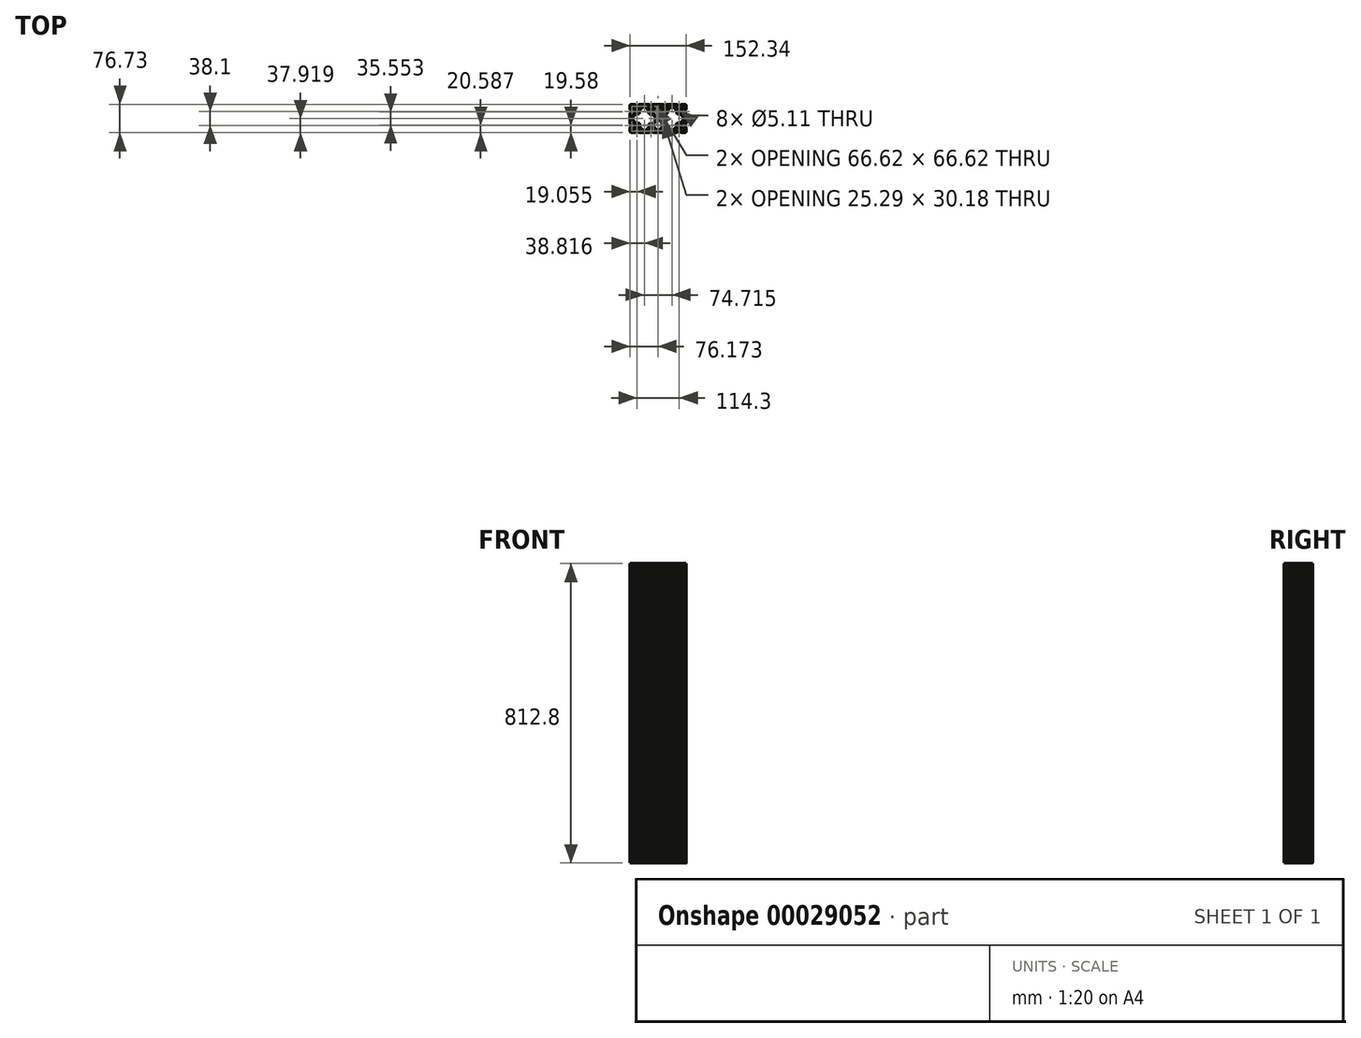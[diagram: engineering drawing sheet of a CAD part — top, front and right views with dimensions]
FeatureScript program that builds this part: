
annotation { "Feature Type Name" : "Feature", "Feature Type Description" : "" }
export const myFeature = defineFeature(function(context is Context, id is Id, definition is map)
    precondition{}
    {
        {
            var Q0;
            Q0=qCreatedBy(makeId("Top.planeOp"),FACE);
            var sketch = newSketch(context, id + "F0", { "sketchPlane" : qUnion([Q0])});
            skLineSegment(sketch, "E0", {"start": v(5.37, 0) * mm, "end": v(1.16, 0) * mm});
            skArc(sketch, "E1", {"start": v(0, 0) * mm, "mid": v(0.58, -0.58) * mm, "end": v(1.16, 0) * mm});
            skLineSegment(sketch, "E2", {"start": v(0, 0) * mm, "end": v(-4.73, 0) * mm});
            skArc(sketch, "E3", {"start": v(-5.9, 0) * mm, "mid": v(-5.3, -0.58) * mm, "end": v(-4.73, 0) * mm});
            skLineSegment(sketch, "E4", {"start": v(-5.9, 0) * mm, "end": v(-7.67, 0) * mm});
            skLineSegment(sketch, "E5", {"start": v(-7.53, -4.06) * mm, "end": v(-4.6, -4.06) * mm});
            skArc(sketch, "E6", {"start": v(-7.67, 0) * mm, "mid": v(-9.7, -2.1) * mm, "end": v(-7.53, -4.06) * mm});
            skLineSegment(sketch, "E7", {"start": v(-8.46, -10.87) * mm, "end": v(-3.58, -6) * mm});
            skArc(sketch, "E8", {"start": v(-3.58, -6) * mm, "mid": v(-3.37, -4.65) * mm, "end": v(-4.6, -4.06) * mm});
            skLineSegment(sketch, "E9", {"start": v(-11.33, -12.06) * mm, "end": v(-13.53, -12.06) * mm});
            skPoint(sketch, "E10.visualSharp", {"position": v(-9.65, -12.06) * mm});
            skArc(sketch, "E10.filletArc", {"start": v(-11.33, -12.06) * mm, "mid": v(-9.77, -11.75) * mm, "end": v(-8.46, -10.87) * mm});
            skArc(sketch, "E11.MirrorCS", {"start": v(-27.06, 0) * mm, "mid": v(-27.64, -0.58) * mm, "end": v(-28.22, 0) * mm});
            skArc(sketch, "E12.MirrorCS", {"start": v(-21.17, 0) * mm, "mid": v(-21.75, -0.58) * mm, "end": v(-22.33, 0) * mm});
            skPoint(sketch, "E13.MirrorP", {"position": v(-17.41, -12.06) * mm});
            skArc(sketch, "E14.MirrorCS", {"start": v(-15.73, -12.06) * mm, "mid": v(-17.28, -11.75) * mm, "end": v(-18.6, -10.87) * mm});
            skLineSegment(sketch, "E15.MirrorCS", {"start": v(-15.73, -12.06) * mm, "end": v(-13.53, -12.06) * mm});
            skArc(sketch, "E16.MirrorCS", {"start": v(-23.48, -6) * mm, "mid": v(-23.68, -4.65) * mm, "end": v(-22.46, -4.06) * mm});
            skLineSegment(sketch, "E17.MirrorCS", {"start": v(-18.6, -10.87) * mm, "end": v(-23.48, -6) * mm});
            skArc(sketch, "E18.MirrorCS", {"start": v(-19.4, 0) * mm, "mid": v(-17.36, -2.1) * mm, "end": v(-19.52, -4.06) * mm});
            skLineSegment(sketch, "E19.MirrorCS", {"start": v(-19.52, -4.06) * mm, "end": v(-22.46, -4.06) * mm});
            skLineSegment(sketch, "E20.MirrorCS", {"start": v(-27.06, 0) * mm, "end": v(-22.33, 0) * mm});
            skLineSegment(sketch, "E21.MirrorCS", {"start": v(-21.17, 0) * mm, "end": v(-19.4, 0) * mm});
            skLineSegment(sketch, "E22.MirrorCS", {"start": v(22.07, -12.06) * mm, "end": v(24.27, -12.06) * mm});
            skLineSegment(sketch, "E23.MirrorCS", {"start": v(26.47, -12.06) * mm, "end": v(24.27, -12.06) * mm});
            skArc(sketch, "E24.MirrorCS", {"start": v(22.07, -12.06) * mm, "mid": v(20.52, -11.75) * mm, "end": v(19.2, -10.87) * mm});
            skArc(sketch, "E25.MirrorCS", {"start": v(26.47, -12.06) * mm, "mid": v(28.03, -11.75) * mm, "end": v(29.35, -10.87) * mm});
            skPoint(sketch, "E26.MirrorP", {"position": v(20.39, -12.06) * mm});
            skPoint(sketch, "E27.MirrorP", {"position": v(28.16, -12.06) * mm});
            skArc(sketch, "E28.MirrorCS", {"start": v(16.63, 0) * mm, "mid": v(16.05, -0.58) * mm, "end": v(15.47, 0) * mm});
            skLineSegment(sketch, "E29.MirrorCS", {"start": v(16.63, 0) * mm, "end": v(18.4, 0) * mm});
            skArc(sketch, "E30.MirrorCS", {"start": v(31.91, 0) * mm, "mid": v(32.5, -0.58) * mm, "end": v(33.07, 0) * mm});
            skArc(sketch, "E31.MirrorCS", {"start": v(10.74, 0) * mm, "mid": v(10.16, -0.58) * mm, "end": v(9.58, 0) * mm});
            skArc(sketch, "E32.MirrorCS", {"start": v(14.32, -6) * mm, "mid": v(14.12, -4.65) * mm, "end": v(15.34, -4.06) * mm});
            skLineSegment(sketch, "E33.MirrorCS", {"start": v(31.91, 0) * mm, "end": v(30.14, 0) * mm});
            skArc(sketch, "E34.MirrorCS", {"start": v(37.8, 0) * mm, "mid": v(38.38, -0.58) * mm, "end": v(38.96, 0) * mm});
            skLineSegment(sketch, "E35.MirrorCS", {"start": v(10.74, 0) * mm, "end": v(15.47, 0) * mm});
            skLineSegment(sketch, "E36.MirrorCS", {"start": v(18.28, -4.06) * mm, "end": v(15.34, -4.06) * mm});
            skArc(sketch, "E37.MirrorCS", {"start": v(34.22, -6) * mm, "mid": v(34.43, -4.65) * mm, "end": v(33.2, -4.06) * mm});
            skLineSegment(sketch, "E38.MirrorCS", {"start": v(19.2, -10.87) * mm, "end": v(14.32, -6) * mm});
            skArc(sketch, "E39.MirrorCS", {"start": v(30.14, 0) * mm, "mid": v(28.1, -2.1) * mm, "end": v(30.27, -4.06) * mm});
            skLineSegment(sketch, "E40.MirrorCS", {"start": v(37.8, 0) * mm, "end": v(33.07, 0) * mm});
            skLineSegment(sketch, "E41.MirrorCS", {"start": v(5.37, 0) * mm, "end": v(9.58, 0) * mm});
            skLineSegment(sketch, "E42.MirrorCS", {"start": v(29.35, -10.87) * mm, "end": v(34.22, -6) * mm});
            skLineSegment(sketch, "E43.MirrorCS", {"start": v(43.17, 0) * mm, "end": v(38.96, 0) * mm});
            skLineSegment(sketch, "E44.MirrorCS", {"start": v(30.27, -4.06) * mm, "end": v(33.2, -4.06) * mm});
            skArc(sketch, "E45.MirrorCS", {"start": v(18.4, 0) * mm, "mid": v(20.44, -2.1) * mm, "end": v(18.28, -4.06) * mm});
            skArc(sketch, "E46.MirrorCS", {"start": v(108.22, 0) * mm, "mid": v(108.8, -0.58) * mm, "end": v(109.39, 0) * mm});
            skLineSegment(sketch, "E47.MirrorCS", {"start": v(108.22, 0) * mm, "end": v(106.45, 0) * mm});
            skArc(sketch, "E48.MirrorCS", {"start": v(114.11, 0) * mm, "mid": v(114.7, -0.58) * mm, "end": v(115.28, 0) * mm});
            skArc(sketch, "E49.MirrorCS", {"start": v(97.68, -12.06) * mm, "mid": v(96.12, -11.75) * mm, "end": v(94.8, -10.87) * mm});
            skLineSegment(sketch, "E50.MirrorCS", {"start": v(114.11, 0) * mm, "end": v(109.39, 0) * mm});
            skArc(sketch, "E51.MirrorCS", {"start": v(102.79, -12.06) * mm, "mid": v(104.34, -11.75) * mm, "end": v(105.66, -10.87) * mm});
            skArc(sketch, "E52.MirrorCS", {"start": v(106.45, 0) * mm, "mid": v(104.42, -2.1) * mm, "end": v(106.58, -4.06) * mm});
            skLineSegment(sketch, "E53.MirrorCS", {"start": v(106.58, -4.06) * mm, "end": v(109.52, -4.06) * mm});
            skArc(sketch, "E54.MirrorCS", {"start": v(110.54, -6) * mm, "mid": v(110.74, -4.65) * mm, "end": v(109.52, -4.06) * mm});
            skArc(sketch, "E55.MirrorCS", {"start": v(94.01, 0) * mm, "mid": v(96.04, -2.1) * mm, "end": v(93.88, -4.06) * mm});
            skLineSegment(sketch, "E56.MirrorCS", {"start": v(105.66, -10.87) * mm, "end": v(110.54, -6) * mm});
            skPoint(sketch, "E57.MirrorP", {"position": v(103.76, -12.06) * mm});
            skArc(sketch, "E58.MirrorCS", {"start": v(86.35, 0) * mm, "mid": v(85.76, -0.58) * mm, "end": v(85.18, 0) * mm});
            skArc(sketch, "E59.MirrorCS", {"start": v(92.24, 0) * mm, "mid": v(91.66, -0.58) * mm, "end": v(91.07, 0) * mm});
            skArc(sketch, "E60.MirrorCS", {"start": v(48.55, 0) * mm, "mid": v(47.96, -0.58) * mm, "end": v(47.38, 0) * mm});
            skArc(sketch, "E61.MirrorCS", {"start": v(54.44, 0) * mm, "mid": v(53.85, -0.58) * mm, "end": v(53.27, 0) * mm});
            skLineSegment(sketch, "E62.MirrorCS", {"start": v(86.35, 0) * mm, "end": v(91.07, 0) * mm});
            skLineSegment(sketch, "E63.MirrorCS", {"start": v(69.71, 0) * mm, "end": v(67.94, 0) * mm});
            skLineSegment(sketch, "E64.MirrorCS", {"start": v(43.17, 0) * mm, "end": v(47.38, 0) * mm});
            skArc(sketch, "E65.MirrorCS", {"start": v(69.71, 0) * mm, "mid": v(70.3, -0.58) * mm, "end": v(70.88, 0) * mm});
            skLineSegment(sketch, "E66.MirrorCS", {"start": v(92.24, 0) * mm, "end": v(94.01, 0) * mm});
            skLineSegment(sketch, "E67.MirrorCS", {"start": v(93.88, -4.06) * mm, "end": v(90.94, -4.06) * mm});
            skLineSegment(sketch, "E68.MirrorCS", {"start": v(94.8, -10.87) * mm, "end": v(89.92, -6) * mm});
            skArc(sketch, "E69.MirrorCS", {"start": v(75.6, 0) * mm, "mid": v(76.18, -0.58) * mm, "end": v(76.77, 0) * mm});
            skArc(sketch, "E70.MirrorCS", {"start": v(89.92, -6) * mm, "mid": v(89.72, -4.65) * mm, "end": v(90.94, -4.06) * mm});
            skLineSegment(sketch, "E71.MirrorCS", {"start": v(75.6, 0) * mm, "end": v(70.88, 0) * mm});
            skLineSegment(sketch, "E72.MirrorCS", {"start": v(48.55, 0) * mm, "end": v(53.27, 0) * mm});
            skArc(sketch, "E73.MirrorCS", {"start": v(64.27, -12.06) * mm, "mid": v(65.83, -11.75) * mm, "end": v(67.15, -10.87) * mm});
            skArc(sketch, "E74.MirrorCS", {"start": v(59.87, -12.06) * mm, "mid": v(58.32, -11.75) * mm, "end": v(57, -10.87) * mm});
            skLineSegment(sketch, "E75.MirrorCS", {"start": v(64.27, -12.06) * mm, "end": v(62.07, -12.06) * mm});
            skLineSegment(sketch, "E76.MirrorCS", {"start": v(54.44, 0) * mm, "end": v(56.21, 0) * mm});
            skLineSegment(sketch, "E77.MirrorCS", {"start": v(59.87, -12.06) * mm, "end": v(62.07, -12.06) * mm});
            skLineSegment(sketch, "E78.MirrorCS", {"start": v(56.08, -4.06) * mm, "end": v(53.14, -4.06) * mm});
            skArc(sketch, "E79.MirrorCS", {"start": v(52.12, -6) * mm, "mid": v(51.92, -4.65) * mm, "end": v(53.14, -4.06) * mm});
            skLineSegment(sketch, "E80.MirrorCS", {"start": v(68.07, -4.06) * mm, "end": v(71, -4.06) * mm});
            skLineSegment(sketch, "E81.MirrorCS", {"start": v(57, -10.87) * mm, "end": v(52.12, -6) * mm});
            skLineSegment(sketch, "E82.MirrorCS", {"start": v(67.15, -10.87) * mm, "end": v(72.03, -6) * mm});
            skArc(sketch, "E83.MirrorCS", {"start": v(56.21, 0) * mm, "mid": v(58.24, -2.1) * mm, "end": v(56.08, -4.06) * mm});
            skLineSegment(sketch, "E84.MirrorCS", {"start": v(80.97, 0) * mm, "end": v(76.77, 0) * mm});
            skLineSegment(sketch, "E85.MirrorCS", {"start": v(80.97, 0) * mm, "end": v(85.18, 0) * mm});
            skArc(sketch, "E86.MirrorCS", {"start": v(72.03, -6) * mm, "mid": v(72.23, -4.65) * mm, "end": v(71, -4.06) * mm});
            skArc(sketch, "E87.MirrorCS", {"start": v(67.94, 0) * mm, "mid": v(65.9, -2.1) * mm, "end": v(68.07, -4.06) * mm});
            skPoint(sketch, "E88.MirrorP", {"position": v(96, -12.06) * mm});
            skPoint(sketch, "E89.MirrorP", {"position": v(65.96, -12.06) * mm});
            skPoint(sketch, "E90.MirrorP", {"position": v(58.2, -12.06) * mm});
            skPoint(sketch, "E91.end.orphan", {"position": v(43.17, -22.8) * mm});
            skLineSegment(sketch, "E92", {"start": v(115.28, 0) * mm, "end": v(115.28, 0) * mm});
            skPoint(sketch, "E93.visualSharp", {"position": v(119.34, 0) * mm});
            skArc(sketch, "E93.filletArc", {"start": v(118.15, -1.2) * mm, "mid": v(116.83, -0.3) * mm, "end": v(115.28, 0) * mm});
            skLineSegment(sketch, "E94", {"start": v(97.68, -12.06) * mm, "end": v(102.79, -12.06) * mm});
            skArc(sketch, "E95.MirrorCS", {"start": v(119.34, -5.23) * mm, "mid": v(118.76, -4.65) * mm, "end": v(119.34, -4.06) * mm});
            skArc(sketch, "E96.MirrorCS", {"start": v(113.35, -29.42) * mm, "mid": v(114.69, -29.62) * mm, "end": v(115.28, -28.4) * mm});
            skLineSegment(sketch, "E97.MirrorCS", {"start": v(119.34, -11.12) * mm, "end": v(119.34, -12.9) * mm});
            skArc(sketch, "E98.MirrorCS", {"start": v(119.34, -11.12) * mm, "mid": v(118.76, -10.54) * mm, "end": v(119.34, -9.95) * mm});
            skLineSegment(sketch, "E99.MirrorCS", {"start": v(115.28, -25.46) * mm, "end": v(115.28, -28.4) * mm});
            skLineSegment(sketch, "E100.MirrorCS", {"start": v(119.34, -5.23) * mm, "end": v(119.34, -9.95) * mm});
            skArc(sketch, "E101.MirrorCS", {"start": v(119.34, -33) * mm, "mid": v(118.76, -33.58) * mm, "end": v(119.34, -34.16) * mm});
            skLineSegment(sketch, "E102.MirrorCS", {"start": v(115.28, -12.76) * mm, "end": v(115.28, -9.82) * mm});
            skArc(sketch, "E103.MirrorCS", {"start": v(107.28, -21.67) * mm, "mid": v(107.59, -23.22) * mm, "end": v(108.47, -24.54) * mm});
            skLineSegment(sketch, "E104.MirrorCS", {"start": v(119.34, -27.1) * mm, "end": v(119.34, -25.33) * mm});
            skLineSegment(sketch, "E105.MirrorCS", {"start": v(108.47, -13.68) * mm, "end": v(113.35, -8.8) * mm});
            skLineSegment(sketch, "E106.MirrorCS", {"start": v(119.34, -33) * mm, "end": v(119.34, -28.27) * mm});
            skArc(sketch, "E107.MirrorCS", {"start": v(113.35, -8.8) * mm, "mid": v(114.69, -8.6) * mm, "end": v(115.28, -9.82) * mm});
            skArc(sketch, "E108.MirrorCS", {"start": v(119.34, -27.1) * mm, "mid": v(118.76, -27.69) * mm, "end": v(119.34, -28.27) * mm});
            skArc(sketch, "E109.MirrorCS", {"start": v(107.28, -16.56) * mm, "mid": v(107.59, -15) * mm, "end": v(108.47, -13.68) * mm});
            skLineSegment(sketch, "E110.MirrorCS", {"start": v(107.28, -21.67) * mm, "end": v(107.28, -16.56) * mm});
            skArc(sketch, "E111.MirrorCS", {"start": v(118.15, -1.2) * mm, "mid": v(119.03, -2.5) * mm, "end": v(119.34, -4.06) * mm});
            skLineSegment(sketch, "E112.MirrorCS", {"start": v(119.34, -38.37) * mm, "end": v(119.34, -34.16) * mm});
            skArc(sketch, "E113.MirrorCS", {"start": v(119.34, -12.9) * mm, "mid": v(117.24, -14.92) * mm, "end": v(115.28, -12.76) * mm});
            skArc(sketch, "E114.MirrorCS", {"start": v(119.34, -25.33) * mm, "mid": v(117.24, -23.3) * mm, "end": v(115.28, -25.46) * mm});
            skLineSegment(sketch, "E115.MirrorCS", {"start": v(108.47, -24.54) * mm, "end": v(113.35, -29.42) * mm});
            skPoint(sketch, "E116.MirrorP", {"position": v(107.28, -15.58) * mm});
            skPoint(sketch, "E117.MirrorP", {"position": v(107.28, -23.35) * mm});
            skLineSegment(sketch, "E118.MirrorCS", {"start": v(-28.94, -12.76) * mm, "end": v(-28.94, -9.82) * mm});
            skArc(sketch, "E119.MirrorCS", {"start": v(-27, -8.8) * mm, "mid": v(-28.34, -8.6) * mm, "end": v(-28.94, -9.82) * mm});
            skLineSegment(sketch, "E120.MirrorCS", {"start": v(-22.12, -13.68) * mm, "end": v(-27, -8.8) * mm});
            skArc(sketch, "E121.MirrorCS", {"start": v(-20.93, -16.56) * mm, "mid": v(-21.24, -15) * mm, "end": v(-22.12, -13.68) * mm});
            skArc(sketch, "E122.MirrorCS", {"start": v(-27, -29.42) * mm, "mid": v(-28.34, -29.62) * mm, "end": v(-28.94, -28.4) * mm});
            skArc(sketch, "E123.MirrorCS", {"start": v(-20.93, -21.67) * mm, "mid": v(-21.24, -23.22) * mm, "end": v(-22.12, -24.54) * mm});
            skLineSegment(sketch, "E124.MirrorCS", {"start": v(-28.94, -25.46) * mm, "end": v(-28.94, -28.4) * mm});
            skPoint(sketch, "E125.MirrorP", {"position": v(-20.93, -15.58) * mm});
            skPoint(sketch, "E126.MirrorP", {"position": v(-20.93, -23.35) * mm});
            skLineSegment(sketch, "E127.MirrorCS", {"start": v(-22.12, -24.54) * mm, "end": v(-27, -29.42) * mm});
            skLineSegment(sketch, "E128.MirrorCS", {"start": v(-20.93, -21.67) * mm, "end": v(-20.93, -16.56) * mm});
            skArc(sketch, "E129.MirrorCS", {"start": v(-33, -11.12) * mm, "mid": v(-32.41, -10.54) * mm, "end": v(-33, -9.95) * mm});
            skArc(sketch, "E130.MirrorCS", {"start": v(-33, -27.1) * mm, "mid": v(-32.41, -27.69) * mm, "end": v(-33, -28.27) * mm});
            skLineSegment(sketch, "E131.MirrorCS", {"start": v(-33, -27.1) * mm, "end": v(-33, -25.33) * mm});
            skLineSegment(sketch, "E132.MirrorCS", {"start": v(-33, -11.12) * mm, "end": v(-33, -12.9) * mm});
            skArc(sketch, "E133.MirrorCS", {"start": v(-31.8, -1.2) * mm, "mid": v(-32.69, -2.5) * mm, "end": v(-33, -4.06) * mm});
            skArc(sketch, "E134.MirrorCS", {"start": v(-33, -5.23) * mm, "mid": v(-32.41, -4.65) * mm, "end": v(-33, -4.06) * mm});
            skArc(sketch, "E135.MirrorCS", {"start": v(-33, -33) * mm, "mid": v(-32.41, -33.58) * mm, "end": v(-33, -34.16) * mm});
            skLineSegment(sketch, "E136.MirrorCS", {"start": v(-33, -38.37) * mm, "end": v(-33, -34.16) * mm});
            skArc(sketch, "E137.MirrorCS", {"start": v(-33, -25.33) * mm, "mid": v(-30.9, -23.3) * mm, "end": v(-28.94, -25.46) * mm});
            skLineSegment(sketch, "E138.MirrorCS", {"start": v(-33, -5.23) * mm, "end": v(-33, -9.95) * mm});
            skLineSegment(sketch, "E139.MirrorCS", {"start": v(-33, -33) * mm, "end": v(-33, -28.27) * mm});
            skArc(sketch, "E140.MirrorCS", {"start": v(-33, -12.9) * mm, "mid": v(-30.9, -14.92) * mm, "end": v(-28.94, -12.76) * mm});
            skArc(sketch, "E141.MirrorCS", {"start": v(-31.8, -1.2) * mm, "mid": v(-30.49, -0.3) * mm, "end": v(-28.93, 0) * mm});
            skLineSegment(sketch, "E142", {"start": v(-28.93, 0) * mm, "end": v(-28.22, 0) * mm});
            skArc(sketch, "E143.MirrorCS", {"start": v(119.34, -43.74) * mm, "mid": v(118.76, -43.16) * mm, "end": v(119.34, -42.58) * mm});
            skLineSegment(sketch, "E144.MirrorCS", {"start": v(-15.73, -64.67) * mm, "end": v(-13.53, -64.67) * mm});
            skArc(sketch, "E145.MirrorCS", {"start": v(0, -76.73) * mm, "mid": v(0.58, -76.15) * mm, "end": v(1.16, -76.73) * mm});
            skLineSegment(sketch, "E146.MirrorCS", {"start": v(37.8, -76.73) * mm, "end": v(33.07, -76.73) * mm});
            skArc(sketch, "E147.MirrorCS", {"start": v(37.8, -76.73) * mm, "mid": v(38.38, -76.15) * mm, "end": v(38.96, -76.73) * mm});
            skLineSegment(sketch, "E148.MirrorCS", {"start": v(-7.53, -72.67) * mm, "end": v(-4.6, -72.67) * mm});
            skArc(sketch, "E149.MirrorCS", {"start": v(54.44, -76.73) * mm, "mid": v(53.85, -76.15) * mm, "end": v(53.27, -76.73) * mm});
            skLineSegment(sketch, "E150.MirrorCS", {"start": v(26.47, -64.67) * mm, "end": v(24.27, -64.67) * mm});
            skLineSegment(sketch, "E151.MirrorCS", {"start": v(59.87, -64.67) * mm, "end": v(62.07, -64.67) * mm});
            skArc(sketch, "E152.MirrorCS", {"start": v(119.34, -71.5) * mm, "mid": v(118.76, -72.09) * mm, "end": v(119.34, -72.67) * mm});
            skArc(sketch, "E153.MirrorCS", {"start": v(86.35, -76.73) * mm, "mid": v(85.76, -76.15) * mm, "end": v(85.18, -76.73) * mm});
            skArc(sketch, "E154.MirrorCS", {"start": v(-5.9, -76.73) * mm, "mid": v(-5.3, -76.15) * mm, "end": v(-4.73, -76.73) * mm});
            skArc(sketch, "E155.MirrorCS", {"start": v(114.11, -76.73) * mm, "mid": v(114.7, -76.15) * mm, "end": v(115.28, -76.73) * mm});
            skArc(sketch, "E156.MirrorCS", {"start": v(31.91, -76.73) * mm, "mid": v(32.5, -76.15) * mm, "end": v(33.07, -76.73) * mm});
            skLineSegment(sketch, "E157.MirrorCS", {"start": v(64.27, -64.67) * mm, "end": v(62.07, -64.67) * mm});
            skLineSegment(sketch, "E158.MirrorCS", {"start": v(-5.9, -76.73) * mm, "end": v(-7.67, -76.73) * mm});
            skLineSegment(sketch, "E159.MirrorCS", {"start": v(-11.33, -64.67) * mm, "end": v(-13.53, -64.67) * mm});
            skLineSegment(sketch, "E160.MirrorCS", {"start": v(31.91, -76.73) * mm, "end": v(30.14, -76.73) * mm});
            skLineSegment(sketch, "E161.MirrorCS", {"start": v(22.07, -64.67) * mm, "end": v(24.27, -64.67) * mm});
            skArc(sketch, "E162.MirrorCS", {"start": v(-33, -71.5) * mm, "mid": v(-32.41, -72.09) * mm, "end": v(-33, -72.67) * mm});
            skArc(sketch, "E163.MirrorCS", {"start": v(-7.67, -76.73) * mm, "mid": v(-9.7, -74.64) * mm, "end": v(-7.53, -72.67) * mm});
            skLineSegment(sketch, "E164.MirrorCS", {"start": v(-33, -71.5) * mm, "end": v(-33, -66.78) * mm});
            skArc(sketch, "E165.MirrorCS", {"start": v(119.34, -65.62) * mm, "mid": v(118.76, -66.2) * mm, "end": v(119.34, -66.78) * mm});
            skLineSegment(sketch, "E166.MirrorCS", {"start": v(-21.17, -76.73) * mm, "end": v(-19.4, -76.73) * mm});
            skArc(sketch, "E167.MirrorCS", {"start": v(-27, -47.32) * mm, "mid": v(-28.34, -47.11) * mm, "end": v(-28.94, -48.34) * mm});
            skLineSegment(sketch, "E168.MirrorCS", {"start": v(119.34, -49.63) * mm, "end": v(119.34, -51.4) * mm});
            skArc(sketch, "E169.MirrorCS", {"start": v(75.6, -76.73) * mm, "mid": v(76.18, -76.15) * mm, "end": v(76.77, -76.73) * mm});
            skLineSegment(sketch, "E170.MirrorCS", {"start": v(-20.93, -55.07) * mm, "end": v(-20.93, -60.18) * mm});
            skArc(sketch, "E171.MirrorCS", {"start": v(-15.73, -64.67) * mm, "mid": v(-17.28, -64.98) * mm, "end": v(-18.6, -65.86) * mm});
            skLineSegment(sketch, "E172.MirrorCS", {"start": v(48.55, -76.73) * mm, "end": v(53.27, -76.73) * mm});
            skArc(sketch, "E173.MirrorCS", {"start": v(108.22, -76.73) * mm, "mid": v(108.8, -76.15) * mm, "end": v(109.39, -76.73) * mm});
            skArc(sketch, "E174.MirrorCS", {"start": v(-27, -67.93) * mm, "mid": v(-28.34, -68.13) * mm, "end": v(-28.94, -66.9) * mm});
            skArc(sketch, "E175.MirrorCS", {"start": v(119.34, -49.63) * mm, "mid": v(118.76, -49.05) * mm, "end": v(119.34, -48.47) * mm});
            skLineSegment(sketch, "E176.MirrorCS", {"start": v(86.35, -76.73) * mm, "end": v(91.07, -76.73) * mm});
            skArc(sketch, "E177.MirrorCS", {"start": v(118.15, -75.54) * mm, "mid": v(116.83, -76.42) * mm, "end": v(115.28, -76.73) * mm});
            skLineSegment(sketch, "E178.MirrorCS", {"start": v(93.88, -72.67) * mm, "end": v(90.94, -72.67) * mm});
            skArc(sketch, "E179.MirrorCS", {"start": v(59.87, -64.67) * mm, "mid": v(58.32, -64.98) * mm, "end": v(57, -65.86) * mm});
            skLineSegment(sketch, "E180.MirrorCS", {"start": v(114.11, -76.73) * mm, "end": v(109.39, -76.73) * mm});
            skLineSegment(sketch, "E181.MirrorCS", {"start": v(54.44, -76.73) * mm, "end": v(56.21, -76.73) * mm});
            skArc(sketch, "E182.MirrorCS", {"start": v(118.15, -75.54) * mm, "mid": v(119.03, -74.23) * mm, "end": v(119.34, -72.67) * mm});
            skArc(sketch, "E183.MirrorCS", {"start": v(26.47, -64.67) * mm, "mid": v(28.03, -64.98) * mm, "end": v(29.35, -65.86) * mm});
            skLineSegment(sketch, "E184.MirrorCS", {"start": v(43.17, -76.73) * mm, "end": v(38.96, -76.73) * mm});
            skLineSegment(sketch, "E185.MirrorCS", {"start": v(-33, -49.63) * mm, "end": v(-33, -51.4) * mm});
            skArc(sketch, "E186.MirrorCS", {"start": v(48.55, -76.73) * mm, "mid": v(47.96, -76.15) * mm, "end": v(47.38, -76.73) * mm});
            skLineSegment(sketch, "E187.MirrorCS", {"start": v(119.34, -65.62) * mm, "end": v(119.34, -63.84) * mm});
            skArc(sketch, "E188.MirrorCS", {"start": v(89.92, -70.74) * mm, "mid": v(89.72, -72.08) * mm, "end": v(90.94, -72.67) * mm});
            skArc(sketch, "E189.MirrorCS", {"start": v(92.24, -76.73) * mm, "mid": v(91.66, -76.15) * mm, "end": v(91.07, -76.73) * mm});
            skLineSegment(sketch, "E190.MirrorCS", {"start": v(107.28, -55.07) * mm, "end": v(107.28, -60.18) * mm});
            skArc(sketch, "E191.MirrorCS", {"start": v(-33, -49.63) * mm, "mid": v(-32.41, -49.05) * mm, "end": v(-33, -48.47) * mm});
            skArc(sketch, "E192.MirrorCS", {"start": v(-27.06, -76.73) * mm, "mid": v(-27.64, -76.15) * mm, "end": v(-28.22, -76.73) * mm});
            skLineSegment(sketch, "E193.MirrorCS", {"start": v(69.71, -76.73) * mm, "end": v(67.94, -76.73) * mm});
            skArc(sketch, "E194.MirrorCS", {"start": v(-19.4, -76.73) * mm, "mid": v(-17.36, -74.64) * mm, "end": v(-19.52, -72.67) * mm});
            skArc(sketch, "E195.MirrorCS", {"start": v(34.22, -70.74) * mm, "mid": v(34.43, -72.08) * mm, "end": v(33.2, -72.67) * mm});
            skArc(sketch, "E196.MirrorCS", {"start": v(16.63, -76.73) * mm, "mid": v(16.05, -76.15) * mm, "end": v(15.47, -76.73) * mm});
            skArc(sketch, "E197.MirrorCS", {"start": v(69.71, -76.73) * mm, "mid": v(70.3, -76.15) * mm, "end": v(70.88, -76.73) * mm});
            skLineSegment(sketch, "E198.MirrorCS", {"start": v(0, -76.73) * mm, "end": v(-4.73, -76.73) * mm});
            skArc(sketch, "E199.MirrorCS", {"start": v(10.74, -76.73) * mm, "mid": v(10.16, -76.15) * mm, "end": v(9.58, -76.73) * mm});
            skLineSegment(sketch, "E200.MirrorCS", {"start": v(119.34, -43.74) * mm, "end": v(119.34, -48.47) * mm});
            skLineSegment(sketch, "E201.MirrorCS", {"start": v(-28.94, -51.27) * mm, "end": v(-28.94, -48.34) * mm});
            skLineSegment(sketch, "E202.MirrorCS", {"start": v(43.17, -76.73) * mm, "end": v(47.38, -76.73) * mm});
            skLineSegment(sketch, "E203.MirrorCS", {"start": v(-28.93, -76.73) * mm, "end": v(-28.22, -76.73) * mm});
            skLineSegment(sketch, "E204.MirrorCS", {"start": v(-8.46, -65.86) * mm, "end": v(-3.58, -70.74) * mm});
            skArc(sketch, "E205.MirrorCS", {"start": v(102.79, -64.67) * mm, "mid": v(104.34, -64.98) * mm, "end": v(105.66, -65.86) * mm});
            skLineSegment(sketch, "E206.MirrorCS", {"start": v(10.74, -76.73) * mm, "end": v(15.47, -76.73) * mm});
            skArc(sketch, "E207.MirrorCS", {"start": v(-33, -65.62) * mm, "mid": v(-32.41, -66.2) * mm, "end": v(-33, -66.78) * mm});
            skArc(sketch, "E208.MirrorCS", {"start": v(-11.33, -64.67) * mm, "mid": v(-9.77, -64.98) * mm, "end": v(-8.46, -65.86) * mm});
            skLineSegment(sketch, "E209.MirrorCS", {"start": v(75.6, -76.73) * mm, "end": v(70.88, -76.73) * mm});
            skLineSegment(sketch, "E210.MirrorCS", {"start": v(-27.06, -76.73) * mm, "end": v(-22.33, -76.73) * mm});
            skArc(sketch, "E211.MirrorCS", {"start": v(-21.17, -76.73) * mm, "mid": v(-21.75, -76.15) * mm, "end": v(-22.33, -76.73) * mm});
            skLineSegment(sketch, "E212.MirrorCS", {"start": v(108.22, -76.73) * mm, "end": v(106.45, -76.73) * mm});
            skArc(sketch, "E213.MirrorCS", {"start": v(-33, -43.74) * mm, "mid": v(-32.41, -43.16) * mm, "end": v(-33, -42.58) * mm});
            skLineSegment(sketch, "E214.MirrorCS", {"start": v(92.24, -76.73) * mm, "end": v(94.01, -76.73) * mm});
            skArc(sketch, "E215.MirrorCS", {"start": v(-3.58, -70.74) * mm, "mid": v(-3.37, -72.08) * mm, "end": v(-4.6, -72.67) * mm});
            skArc(sketch, "E216.MirrorCS", {"start": v(52.12, -70.74) * mm, "mid": v(51.92, -72.08) * mm, "end": v(53.14, -72.67) * mm});
            skArc(sketch, "E217.MirrorCS", {"start": v(113.35, -47.32) * mm, "mid": v(114.69, -47.11) * mm, "end": v(115.28, -48.34) * mm});
            skLineSegment(sketch, "E218.MirrorCS", {"start": v(119.34, -38.37) * mm, "end": v(119.34, -42.58) * mm});
            skLineSegment(sketch, "E219.MirrorCS", {"start": v(-33, -65.62) * mm, "end": v(-33, -63.84) * mm});
            skArc(sketch, "E220.MirrorCS", {"start": v(-33, -63.84) * mm, "mid": v(-30.9, -61.81) * mm, "end": v(-28.94, -63.97) * mm});
            skLineSegment(sketch, "E221.MirrorCS", {"start": v(18.28, -72.67) * mm, "end": v(15.34, -72.67) * mm});
            skLineSegment(sketch, "E222.MirrorCS", {"start": v(115.28, -63.97) * mm, "end": v(115.28, -66.9) * mm});
            skArc(sketch, "E223.MirrorCS", {"start": v(-23.48, -70.74) * mm, "mid": v(-23.68, -72.08) * mm, "end": v(-22.46, -72.67) * mm});
            skLineSegment(sketch, "E224.MirrorCS", {"start": v(105.66, -65.86) * mm, "end": v(110.54, -70.74) * mm});
            skArc(sketch, "E225.MirrorCS", {"start": v(-31.8, -75.54) * mm, "mid": v(-32.69, -74.23) * mm, "end": v(-33, -72.67) * mm});
            skLineSegment(sketch, "E226.MirrorCS", {"start": v(68.07, -72.67) * mm, "end": v(71, -72.67) * mm});
            skArc(sketch, "E227.MirrorCS", {"start": v(-33, -51.4) * mm, "mid": v(-30.9, -53.44) * mm, "end": v(-28.94, -51.27) * mm});
            skArc(sketch, "E228.MirrorCS", {"start": v(119.34, -51.4) * mm, "mid": v(117.24, -53.44) * mm, "end": v(115.28, -51.27) * mm});
            skArc(sketch, "E229.MirrorCS", {"start": v(-20.93, -55.07) * mm, "mid": v(-21.24, -53.51) * mm, "end": v(-22.12, -52.2) * mm});
            skArc(sketch, "E230.MirrorCS", {"start": v(67.94, -76.73) * mm, "mid": v(65.9, -74.64) * mm, "end": v(68.07, -72.67) * mm});
            skArc(sketch, "E231.MirrorCS", {"start": v(119.34, -63.84) * mm, "mid": v(117.24, -61.81) * mm, "end": v(115.28, -63.97) * mm});
            skArc(sketch, "E232.MirrorCS", {"start": v(107.28, -55.07) * mm, "mid": v(107.59, -53.51) * mm, "end": v(108.47, -52.2) * mm});
            skArc(sketch, "E233.MirrorCS", {"start": v(14.32, -70.74) * mm, "mid": v(14.12, -72.08) * mm, "end": v(15.34, -72.67) * mm});
            skArc(sketch, "E234.MirrorCS", {"start": v(97.68, -64.67) * mm, "mid": v(96.12, -64.98) * mm, "end": v(94.8, -65.86) * mm});
            skArc(sketch, "E235.MirrorCS", {"start": v(64.27, -64.67) * mm, "mid": v(65.83, -64.98) * mm, "end": v(67.15, -65.86) * mm});
            skLineSegment(sketch, "E236.MirrorCS", {"start": v(5.37, -76.73) * mm, "end": v(9.58, -76.73) * mm});
            skLineSegment(sketch, "E237.MirrorCS", {"start": v(19.2, -65.86) * mm, "end": v(14.32, -70.74) * mm});
            skArc(sketch, "E238.MirrorCS", {"start": v(110.54, -70.74) * mm, "mid": v(110.74, -72.08) * mm, "end": v(109.52, -72.67) * mm});
            skLineSegment(sketch, "E239.MirrorCS", {"start": v(106.58, -72.67) * mm, "end": v(109.52, -72.67) * mm});
            skArc(sketch, "E240.MirrorCS", {"start": v(113.35, -67.93) * mm, "mid": v(114.69, -68.13) * mm, "end": v(115.28, -66.9) * mm});
            skLineSegment(sketch, "E241.MirrorCS", {"start": v(-19.52, -72.67) * mm, "end": v(-22.46, -72.67) * mm});
            skArc(sketch, "E242.MirrorCS", {"start": v(107.28, -60.18) * mm, "mid": v(107.59, -61.73) * mm, "end": v(108.47, -63.05) * mm});
            skLineSegment(sketch, "E243.MirrorCS", {"start": v(29.35, -65.86) * mm, "end": v(34.22, -70.74) * mm});
            skLineSegment(sketch, "E244.MirrorCS", {"start": v(119.34, -71.5) * mm, "end": v(119.34, -66.78) * mm});
            skLineSegment(sketch, "E245.MirrorCS", {"start": v(16.63, -76.73) * mm, "end": v(18.4, -76.73) * mm});
            skLineSegment(sketch, "E246.MirrorCS", {"start": v(115.28, -51.27) * mm, "end": v(115.28, -48.34) * mm});
            skLineSegment(sketch, "E247.MirrorCS", {"start": v(97.68, -64.67) * mm, "end": v(102.79, -64.67) * mm});
            skArc(sketch, "E248.MirrorCS", {"start": v(72.03, -70.74) * mm, "mid": v(72.23, -72.08) * mm, "end": v(71, -72.67) * mm});
            skArc(sketch, "E249.MirrorCS", {"start": v(94.01, -76.73) * mm, "mid": v(96.04, -74.64) * mm, "end": v(93.88, -72.67) * mm});
            skLineSegment(sketch, "E250.MirrorCS", {"start": v(80.97, -76.73) * mm, "end": v(85.18, -76.73) * mm});
            skLineSegment(sketch, "E251.MirrorCS", {"start": v(-33, -38.37) * mm, "end": v(-33, -42.58) * mm});
            skLineSegment(sketch, "E252.MirrorCS", {"start": v(-28.94, -63.97) * mm, "end": v(-28.94, -66.9) * mm});
            skLineSegment(sketch, "E253.MirrorCS", {"start": v(-22.12, -52.2) * mm, "end": v(-27, -47.32) * mm});
            skLineSegment(sketch, "E254.MirrorCS", {"start": v(80.97, -76.73) * mm, "end": v(76.77, -76.73) * mm});
            skArc(sketch, "E255.MirrorCS", {"start": v(-20.93, -60.18) * mm, "mid": v(-21.24, -61.73) * mm, "end": v(-22.12, -63.05) * mm});
            skArc(sketch, "E256.MirrorCS", {"start": v(-31.8, -75.54) * mm, "mid": v(-30.49, -76.42) * mm, "end": v(-28.93, -76.73) * mm});
            skArc(sketch, "E257.MirrorCS", {"start": v(106.45, -76.73) * mm, "mid": v(104.42, -74.64) * mm, "end": v(106.58, -72.67) * mm});
            skLineSegment(sketch, "E258.MirrorCS", {"start": v(56.08, -72.67) * mm, "end": v(53.14, -72.67) * mm});
            skLineSegment(sketch, "E259.MirrorCS", {"start": v(30.27, -72.67) * mm, "end": v(33.2, -72.67) * mm});
            skLineSegment(sketch, "E260.MirrorCS", {"start": v(94.8, -65.86) * mm, "end": v(89.92, -70.74) * mm});
            skLineSegment(sketch, "E261.MirrorCS", {"start": v(5.37, -76.73) * mm, "end": v(1.16, -76.73) * mm});
            skArc(sketch, "E262.MirrorCS", {"start": v(22.07, -64.67) * mm, "mid": v(20.52, -64.98) * mm, "end": v(19.2, -65.86) * mm});
            skLineSegment(sketch, "E263.MirrorCS", {"start": v(-33, -43.74) * mm, "end": v(-33, -48.47) * mm});
            skLineSegment(sketch, "E264.MirrorCS", {"start": v(108.47, -52.2) * mm, "end": v(113.35, -47.32) * mm});
            skLineSegment(sketch, "E265.MirrorCS", {"start": v(57, -65.86) * mm, "end": v(52.12, -70.74) * mm});
            skPoint(sketch, "E266.MirrorP", {"position": v(-9.65, -64.67) * mm});
            skPoint(sketch, "E267.MirrorP", {"position": v(119.34, -76.73) * mm});
            skArc(sketch, "E268.MirrorCS", {"start": v(18.4, -76.73) * mm, "mid": v(20.44, -74.64) * mm, "end": v(18.28, -72.67) * mm});
            skLineSegment(sketch, "E269.MirrorCS", {"start": v(108.47, -63.05) * mm, "end": v(113.35, -67.93) * mm});
            skLineSegment(sketch, "E270.MirrorCS", {"start": v(115.28, -76.73) * mm, "end": v(115.28, -76.73) * mm});
            skPoint(sketch, "E271.MirrorP", {"position": v(103.76, -64.67) * mm});
            skPoint(sketch, "E272.MirrorP", {"position": v(28.16, -64.67) * mm});
            skPoint(sketch, "E273.MirrorP", {"position": v(107.28, -61.15) * mm});
            skPoint(sketch, "E274.MirrorP", {"position": v(43.17, -53.94) * mm});
            skArc(sketch, "E275.MirrorCS", {"start": v(56.21, -76.73) * mm, "mid": v(58.24, -74.64) * mm, "end": v(56.08, -72.67) * mm});
            skPoint(sketch, "E276.MirrorP", {"position": v(65.96, -64.67) * mm});
            skLineSegment(sketch, "E277.MirrorCS", {"start": v(67.15, -65.86) * mm, "end": v(72.03, -70.74) * mm});
            skPoint(sketch, "E278.MirrorP", {"position": v(-17.41, -64.67) * mm});
            skPoint(sketch, "E279.MirrorP", {"position": v(107.28, -53.38) * mm});
            skLineSegment(sketch, "E280.MirrorCS", {"start": v(-22.12, -63.05) * mm, "end": v(-27, -67.93) * mm});
            skPoint(sketch, "E281.MirrorP", {"position": v(20.39, -64.67) * mm});
            skPoint(sketch, "E282.MirrorP", {"position": v(-20.93, -61.15) * mm});
            skPoint(sketch, "E283.MirrorP", {"position": v(-20.93, -53.38) * mm});
            skLineSegment(sketch, "E284.MirrorCS", {"start": v(-18.6, -65.86) * mm, "end": v(-23.48, -70.74) * mm});
            skPoint(sketch, "E285.MirrorP", {"position": v(58.2, -64.67) * mm});
            skPoint(sketch, "E286.MirrorP", {"position": v(96, -64.67) * mm});
            skArc(sketch, "E287.MirrorCS", {"start": v(30.14, -76.73) * mm, "mid": v(28.1, -74.64) * mm, "end": v(30.27, -72.67) * mm});
            skSolve(sketch);
        }
        {
            var Q0;
            Q0 = qSketchRegion(id + "F0", true);
            extrude(context, id + "F1", {"entities" : qUnion([Q0]), "depth" : 812.8 * mm});
        }
        {
            var Q0;
            Q0=makeQuery(id+"F1.opExtrude","CAP_FACE",FACE,{"disambiguationData":[OSD([sQuery(id+"F0.wireOp",EDGE,"E0"),sQuery(id+"F0.wireOp",EDGE,"E1"),sQuery(id+"F0.wireOp",EDGE,"E2"),sQuery(id+"F0.wireOp",EDGE,"E3"),sQuery(id+"F0.wireOp",EDGE,"E4"),sQuery(id+"F0.wireOp",EDGE,"E5"),sQuery(id+"F0.wireOp",EDGE,"E6"),sQuery(id+"F0.wireOp",EDGE,"E7"),sQuery(id+"F0.wireOp",EDGE,"E8"),sQuery(id+"F0.wireOp",EDGE,"E9"),sQuery(id+"F0.wireOp",EDGE,"E10.filletArc"),sQuery(id+"F0.wireOp",EDGE,"E11.MirrorCS"),sQuery(id+"F0.wireOp",EDGE,"E12.MirrorCS"),sQuery(id+"F0.wireOp",EDGE,"E14.MirrorCS"),sQuery(id+"F0.wireOp",EDGE,"E15.MirrorCS"),sQuery(id+"F0.wireOp",EDGE,"E16.MirrorCS"),sQuery(id+"F0.wireOp",EDGE,"E17.MirrorCS"),sQuery(id+"F0.wireOp",EDGE,"E18.MirrorCS"),sQuery(id+"F0.wireOp",EDGE,"E19.MirrorCS"),sQuery(id+"F0.wireOp",EDGE,"E20.MirrorCS"),sQuery(id+"F0.wireOp",EDGE,"E21.MirrorCS"),sQuery(id+"F0.wireOp",EDGE,"E22.MirrorCS"),sQuery(id+"F0.wireOp",EDGE,"E23.MirrorCS"),sQuery(id+"F0.wireOp",EDGE,"E24.MirrorCS"),sQuery(id+"F0.wireOp",EDGE,"E25.MirrorCS"),sQuery(id+"F0.wireOp",EDGE,"E28.MirrorCS"),sQuery(id+"F0.wireOp",EDGE,"E29.MirrorCS"),sQuery(id+"F0.wireOp",EDGE,"E30.MirrorCS"),sQuery(id+"F0.wireOp",EDGE,"E31.MirrorCS"),sQuery(id+"F0.wireOp",EDGE,"E32.MirrorCS"),sQuery(id+"F0.wireOp",EDGE,"E33.MirrorCS"),sQuery(id+"F0.wireOp",EDGE,"E34.MirrorCS"),sQuery(id+"F0.wireOp",EDGE,"E35.MirrorCS"),sQuery(id+"F0.wireOp",EDGE,"E36.MirrorCS"),sQuery(id+"F0.wireOp",EDGE,"E37.MirrorCS"),sQuery(id+"F0.wireOp",EDGE,"E38.MirrorCS"),sQuery(id+"F0.wireOp",EDGE,"E39.MirrorCS"),sQuery(id+"F0.wireOp",EDGE,"E40.MirrorCS"),sQuery(id+"F0.wireOp",EDGE,"E41.MirrorCS"),sQuery(id+"F0.wireOp",EDGE,"E42.MirrorCS"),sQuery(id+"F0.wireOp",EDGE,"E43.MirrorCS"),sQuery(id+"F0.wireOp",EDGE,"E44.MirrorCS"),sQuery(id+"F0.wireOp",EDGE,"E45.MirrorCS"),sQuery(id+"F0.wireOp",EDGE,"E46.MirrorCS"),sQuery(id+"F0.wireOp",EDGE,"E47.MirrorCS"),sQuery(id+"F0.wireOp",EDGE,"E48.MirrorCS"),sQuery(id+"F0.wireOp",EDGE,"E49.MirrorCS"),sQuery(id+"F0.wireOp",EDGE,"E50.MirrorCS"),sQuery(id+"F0.wireOp",EDGE,"E51.MirrorCS"),sQuery(id+"F0.wireOp",EDGE,"E52.MirrorCS"),sQuery(id+"F0.wireOp",EDGE,"E53.MirrorCS"),sQuery(id+"F0.wireOp",EDGE,"E54.MirrorCS"),sQuery(id+"F0.wireOp",EDGE,"E55.MirrorCS"),sQuery(id+"F0.wireOp",EDGE,"E56.MirrorCS"),sQuery(id+"F0.wireOp",EDGE,"E58.MirrorCS"),sQuery(id+"F0.wireOp",EDGE,"E59.MirrorCS"),sQuery(id+"F0.wireOp",EDGE,"E60.MirrorCS"),sQuery(id+"F0.wireOp",EDGE,"E61.MirrorCS"),sQuery(id+"F0.wireOp",EDGE,"E62.MirrorCS"),sQuery(id+"F0.wireOp",EDGE,"E63.MirrorCS"),sQuery(id+"F0.wireOp",EDGE,"E64.MirrorCS"),sQuery(id+"F0.wireOp",EDGE,"E65.MirrorCS"),sQuery(id+"F0.wireOp",EDGE,"E66.MirrorCS"),sQuery(id+"F0.wireOp",EDGE,"E67.MirrorCS"),sQuery(id+"F0.wireOp",EDGE,"E68.MirrorCS"),sQuery(id+"F0.wireOp",EDGE,"E69.MirrorCS"),sQuery(id+"F0.wireOp",EDGE,"E70.MirrorCS"),sQuery(id+"F0.wireOp",EDGE,"E71.MirrorCS"),sQuery(id+"F0.wireOp",EDGE,"E72.MirrorCS"),sQuery(id+"F0.wireOp",EDGE,"E73.MirrorCS"),sQuery(id+"F0.wireOp",EDGE,"E74.MirrorCS"),sQuery(id+"F0.wireOp",EDGE,"E75.MirrorCS"),sQuery(id+"F0.wireOp",EDGE,"E76.MirrorCS"),sQuery(id+"F0.wireOp",EDGE,"E77.MirrorCS"),sQuery(id+"F0.wireOp",EDGE,"E78.MirrorCS"),sQuery(id+"F0.wireOp",EDGE,"E79.MirrorCS"),sQuery(id+"F0.wireOp",EDGE,"E80.MirrorCS"),sQuery(id+"F0.wireOp",EDGE,"E81.MirrorCS"),sQuery(id+"F0.wireOp",EDGE,"E82.MirrorCS"),sQuery(id+"F0.wireOp",EDGE,"E83.MirrorCS"),sQuery(id+"F0.wireOp",EDGE,"E84.MirrorCS"),sQuery(id+"F0.wireOp",EDGE,"E85.MirrorCS"),sQuery(id+"F0.wireOp",EDGE,"E86.MirrorCS"),sQuery(id+"F0.wireOp",EDGE,"E87.MirrorCS"),sQuery(id+"F0.wireOp",EDGE,"E93.filletArc"),sQuery(id+"F0.wireOp",EDGE,"E94"),sQuery(id+"F0.wireOp",EDGE,"E95.MirrorCS"),sQuery(id+"F0.wireOp",EDGE,"E96.MirrorCS"),sQuery(id+"F0.wireOp",EDGE,"E97.MirrorCS"),sQuery(id+"F0.wireOp",EDGE,"E98.MirrorCS"),sQuery(id+"F0.wireOp",EDGE,"E99.MirrorCS"),sQuery(id+"F0.wireOp",EDGE,"E100.MirrorCS"),sQuery(id+"F0.wireOp",EDGE,"E101.MirrorCS"),sQuery(id+"F0.wireOp",EDGE,"E102.MirrorCS"),sQuery(id+"F0.wireOp",EDGE,"E103.MirrorCS"),sQuery(id+"F0.wireOp",EDGE,"E104.MirrorCS"),sQuery(id+"F0.wireOp",EDGE,"E105.MirrorCS"),sQuery(id+"F0.wireOp",EDGE,"E106.MirrorCS"),sQuery(id+"F0.wireOp",EDGE,"E107.MirrorCS"),sQuery(id+"F0.wireOp",EDGE,"E108.MirrorCS"),sQuery(id+"F0.wireOp",EDGE,"E109.MirrorCS"),sQuery(id+"F0.wireOp",EDGE,"E110.MirrorCS"),sQuery(id+"F0.wireOp",EDGE,"E111.MirrorCS"),sQuery(id+"F0.wireOp",EDGE,"E112.MirrorCS"),sQuery(id+"F0.wireOp",EDGE,"E113.MirrorCS"),sQuery(id+"F0.wireOp",EDGE,"E114.MirrorCS"),sQuery(id+"F0.wireOp",EDGE,"E115.MirrorCS"),sQuery(id+"F0.wireOp",EDGE,"E118.MirrorCS"),sQuery(id+"F0.wireOp",EDGE,"E119.MirrorCS"),sQuery(id+"F0.wireOp",EDGE,"E120.MirrorCS"),sQuery(id+"F0.wireOp",EDGE,"E121.MirrorCS"),sQuery(id+"F0.wireOp",EDGE,"E122.MirrorCS"),sQuery(id+"F0.wireOp",EDGE,"E123.MirrorCS"),sQuery(id+"F0.wireOp",EDGE,"E124.MirrorCS"),sQuery(id+"F0.wireOp",EDGE,"E127.MirrorCS"),sQuery(id+"F0.wireOp",EDGE,"E128.MirrorCS"),sQuery(id+"F0.wireOp",EDGE,"E129.MirrorCS"),sQuery(id+"F0.wireOp",EDGE,"E130.MirrorCS"),sQuery(id+"F0.wireOp",EDGE,"E131.MirrorCS"),sQuery(id+"F0.wireOp",EDGE,"E132.MirrorCS"),sQuery(id+"F0.wireOp",EDGE,"E133.MirrorCS"),sQuery(id+"F0.wireOp",EDGE,"E134.MirrorCS"),sQuery(id+"F0.wireOp",EDGE,"E135.MirrorCS"),sQuery(id+"F0.wireOp",EDGE,"E136.MirrorCS"),sQuery(id+"F0.wireOp",EDGE,"E137.MirrorCS"),sQuery(id+"F0.wireOp",EDGE,"E138.MirrorCS"),sQuery(id+"F0.wireOp",EDGE,"E139.MirrorCS"),sQuery(id+"F0.wireOp",EDGE,"E140.MirrorCS"),sQuery(id+"F0.wireOp",EDGE,"E141.MirrorCS"),sQuery(id+"F0.wireOp",EDGE,"E142"),sQuery(id+"F0.wireOp",EDGE,"E143.MirrorCS"),sQuery(id+"F0.wireOp",EDGE,"E144.MirrorCS"),sQuery(id+"F0.wireOp",EDGE,"E145.MirrorCS"),sQuery(id+"F0.wireOp",EDGE,"E146.MirrorCS"),sQuery(id+"F0.wireOp",EDGE,"E147.MirrorCS"),sQuery(id+"F0.wireOp",EDGE,"E148.MirrorCS"),sQuery(id+"F0.wireOp",EDGE,"E149.MirrorCS"),sQuery(id+"F0.wireOp",EDGE,"E150.MirrorCS"),sQuery(id+"F0.wireOp",EDGE,"E151.MirrorCS"),sQuery(id+"F0.wireOp",EDGE,"E152.MirrorCS"),sQuery(id+"F0.wireOp",EDGE,"E153.MirrorCS"),sQuery(id+"F0.wireOp",EDGE,"E154.MirrorCS"),sQuery(id+"F0.wireOp",EDGE,"E155.MirrorCS"),sQuery(id+"F0.wireOp",EDGE,"E156.MirrorCS"),sQuery(id+"F0.wireOp",EDGE,"E157.MirrorCS"),sQuery(id+"F0.wireOp",EDGE,"E158.MirrorCS"),sQuery(id+"F0.wireOp",EDGE,"E159.MirrorCS"),sQuery(id+"F0.wireOp",EDGE,"E160.MirrorCS"),sQuery(id+"F0.wireOp",EDGE,"E161.MirrorCS"),sQuery(id+"F0.wireOp",EDGE,"E162.MirrorCS"),sQuery(id+"F0.wireOp",EDGE,"E163.MirrorCS"),sQuery(id+"F0.wireOp",EDGE,"E164.MirrorCS"),sQuery(id+"F0.wireOp",EDGE,"E165.MirrorCS"),sQuery(id+"F0.wireOp",EDGE,"E166.MirrorCS"),sQuery(id+"F0.wireOp",EDGE,"E167.MirrorCS"),sQuery(id+"F0.wireOp",EDGE,"E168.MirrorCS"),sQuery(id+"F0.wireOp",EDGE,"E169.MirrorCS"),sQuery(id+"F0.wireOp",EDGE,"E170.MirrorCS"),sQuery(id+"F0.wireOp",EDGE,"E171.MirrorCS"),sQuery(id+"F0.wireOp",EDGE,"E172.MirrorCS"),sQuery(id+"F0.wireOp",EDGE,"E173.MirrorCS"),sQuery(id+"F0.wireOp",EDGE,"E174.MirrorCS"),sQuery(id+"F0.wireOp",EDGE,"E175.MirrorCS"),sQuery(id+"F0.wireOp",EDGE,"E176.MirrorCS"),sQuery(id+"F0.wireOp",EDGE,"E177.MirrorCS"),sQuery(id+"F0.wireOp",EDGE,"E178.MirrorCS"),sQuery(id+"F0.wireOp",EDGE,"E179.MirrorCS"),sQuery(id+"F0.wireOp",EDGE,"E180.MirrorCS"),sQuery(id+"F0.wireOp",EDGE,"E181.MirrorCS"),sQuery(id+"F0.wireOp",EDGE,"E182.MirrorCS"),sQuery(id+"F0.wireOp",EDGE,"E183.MirrorCS"),sQuery(id+"F0.wireOp",EDGE,"E184.MirrorCS"),sQuery(id+"F0.wireOp",EDGE,"E185.MirrorCS"),sQuery(id+"F0.wireOp",EDGE,"E186.MirrorCS"),sQuery(id+"F0.wireOp",EDGE,"E187.MirrorCS"),sQuery(id+"F0.wireOp",EDGE,"E188.MirrorCS"),sQuery(id+"F0.wireOp",EDGE,"E189.MirrorCS"),sQuery(id+"F0.wireOp",EDGE,"E190.MirrorCS"),sQuery(id+"F0.wireOp",EDGE,"E191.MirrorCS"),sQuery(id+"F0.wireOp",EDGE,"E192.MirrorCS"),sQuery(id+"F0.wireOp",EDGE,"E193.MirrorCS"),sQuery(id+"F0.wireOp",EDGE,"E194.MirrorCS"),sQuery(id+"F0.wireOp",EDGE,"E195.MirrorCS"),sQuery(id+"F0.wireOp",EDGE,"E196.MirrorCS"),sQuery(id+"F0.wireOp",EDGE,"E197.MirrorCS"),sQuery(id+"F0.wireOp",EDGE,"E198.MirrorCS"),sQuery(id+"F0.wireOp",EDGE,"E199.MirrorCS"),sQuery(id+"F0.wireOp",EDGE,"E200.MirrorCS"),sQuery(id+"F0.wireOp",EDGE,"E201.MirrorCS"),sQuery(id+"F0.wireOp",EDGE,"E202.MirrorCS"),sQuery(id+"F0.wireOp",EDGE,"E203.MirrorCS"),sQuery(id+"F0.wireOp",EDGE,"E204.MirrorCS"),sQuery(id+"F0.wireOp",EDGE,"E205.MirrorCS"),sQuery(id+"F0.wireOp",EDGE,"E206.MirrorCS"),sQuery(id+"F0.wireOp",EDGE,"E207.MirrorCS"),sQuery(id+"F0.wireOp",EDGE,"E208.MirrorCS"),sQuery(id+"F0.wireOp",EDGE,"E209.MirrorCS"),sQuery(id+"F0.wireOp",EDGE,"E210.MirrorCS"),sQuery(id+"F0.wireOp",EDGE,"E211.MirrorCS"),sQuery(id+"F0.wireOp",EDGE,"E212.MirrorCS"),sQuery(id+"F0.wireOp",EDGE,"E213.MirrorCS"),sQuery(id+"F0.wireOp",EDGE,"E214.MirrorCS"),sQuery(id+"F0.wireOp",EDGE,"E215.MirrorCS"),sQuery(id+"F0.wireOp",EDGE,"E216.MirrorCS"),sQuery(id+"F0.wireOp",EDGE,"E217.MirrorCS"),sQuery(id+"F0.wireOp",EDGE,"E218.MirrorCS"),sQuery(id+"F0.wireOp",EDGE,"E219.MirrorCS"),sQuery(id+"F0.wireOp",EDGE,"E220.MirrorCS"),sQuery(id+"F0.wireOp",EDGE,"E221.MirrorCS"),sQuery(id+"F0.wireOp",EDGE,"E222.MirrorCS"),sQuery(id+"F0.wireOp",EDGE,"E223.MirrorCS"),sQuery(id+"F0.wireOp",EDGE,"E224.MirrorCS"),sQuery(id+"F0.wireOp",EDGE,"E225.MirrorCS"),sQuery(id+"F0.wireOp",EDGE,"E226.MirrorCS"),sQuery(id+"F0.wireOp",EDGE,"E227.MirrorCS"),sQuery(id+"F0.wireOp",EDGE,"E228.MirrorCS"),sQuery(id+"F0.wireOp",EDGE,"E229.MirrorCS"),sQuery(id+"F0.wireOp",EDGE,"E230.MirrorCS"),sQuery(id+"F0.wireOp",EDGE,"E231.MirrorCS"),sQuery(id+"F0.wireOp",EDGE,"E232.MirrorCS"),sQuery(id+"F0.wireOp",EDGE,"E233.MirrorCS"),sQuery(id+"F0.wireOp",EDGE,"E234.MirrorCS"),sQuery(id+"F0.wireOp",EDGE,"E235.MirrorCS"),sQuery(id+"F0.wireOp",EDGE,"E236.MirrorCS"),sQuery(id+"F0.wireOp",EDGE,"E237.MirrorCS"),sQuery(id+"F0.wireOp",EDGE,"E238.MirrorCS"),sQuery(id+"F0.wireOp",EDGE,"E239.MirrorCS"),sQuery(id+"F0.wireOp",EDGE,"E240.MirrorCS"),sQuery(id+"F0.wireOp",EDGE,"E241.MirrorCS"),sQuery(id+"F0.wireOp",EDGE,"E242.MirrorCS"),sQuery(id+"F0.wireOp",EDGE,"E243.MirrorCS"),sQuery(id+"F0.wireOp",EDGE,"E244.MirrorCS"),sQuery(id+"F0.wireOp",EDGE,"E245.MirrorCS"),sQuery(id+"F0.wireOp",EDGE,"E246.MirrorCS"),sQuery(id+"F0.wireOp",EDGE,"E247.MirrorCS"),sQuery(id+"F0.wireOp",EDGE,"E248.MirrorCS"),sQuery(id+"F0.wireOp",EDGE,"E249.MirrorCS"),sQuery(id+"F0.wireOp",EDGE,"E250.MirrorCS"),sQuery(id+"F0.wireOp",EDGE,"E251.MirrorCS"),sQuery(id+"F0.wireOp",EDGE,"E252.MirrorCS"),sQuery(id+"F0.wireOp",EDGE,"E253.MirrorCS"),sQuery(id+"F0.wireOp",EDGE,"E254.MirrorCS"),sQuery(id+"F0.wireOp",EDGE,"E255.MirrorCS"),sQuery(id+"F0.wireOp",EDGE,"E256.MirrorCS"),sQuery(id+"F0.wireOp",EDGE,"E257.MirrorCS"),sQuery(id+"F0.wireOp",EDGE,"E258.MirrorCS"),sQuery(id+"F0.wireOp",EDGE,"E259.MirrorCS"),sQuery(id+"F0.wireOp",EDGE,"E260.MirrorCS"),sQuery(id+"F0.wireOp",EDGE,"E261.MirrorCS"),sQuery(id+"F0.wireOp",EDGE,"E262.MirrorCS"),sQuery(id+"F0.wireOp",EDGE,"E263.MirrorCS"),sQuery(id+"F0.wireOp",EDGE,"E264.MirrorCS"),sQuery(id+"F0.wireOp",EDGE,"E265.MirrorCS"),sQuery(id+"F0.wireOp",EDGE,"E268.MirrorCS"),sQuery(id+"F0.wireOp",EDGE,"E269.MirrorCS"),sQuery(id+"F0.wireOp",EDGE,"E275.MirrorCS"),sQuery(id+"F0.wireOp",EDGE,"E277.MirrorCS"),sQuery(id+"F0.wireOp",EDGE,"E280.MirrorCS"),sQuery(id+"F0.wireOp",EDGE,"E284.MirrorCS"),sQuery(id+"F0.wireOp",EDGE,"E287.MirrorCS")])],"isStart":false});
            var sketch = newSketch(context, id + "F2", { "sketchPlane" : qUnion([Q0])});
            skLineSegment(sketch, "E288", {"start": v(3.94, -5.5) * mm, "end": v(-6.08, -15.52) * mm});
            skLineSegment(sketch, "E289", {"start": v(6.8, -5.5) * mm, "end": v(16.83, -15.52) * mm});
            skLineSegment(sketch, "E290", {"start": v(-7.27, -18.4) * mm, "end": v(-7.27, -22.8) * mm});
            skArc(sketch, "E291.filletArc", {"start": v(-6.08, -15.52) * mm, "mid": v(-6.96, -16.84) * mm, "end": v(-7.27, -18.4) * mm});
            skArc(sketch, "E292.filletArc", {"start": v(-7.95, -25.04) * mm, "mid": v(-7.45, -23.97) * mm, "end": v(-7.27, -22.8) * mm});
            skLineSegment(sketch, "E293", {"start": v(18.02, -18.4) * mm, "end": v(18.02, -22.8) * mm});
            skArc(sketch, "E294.filletArc", {"start": v(18.02, -18.4) * mm, "mid": v(17.7, -16.84) * mm, "end": v(16.83, -15.52) * mm});
            skArc(sketch, "E295.MirrorCS", {"start": v(-14.6, -51.01) * mm, "mid": v(-16.16, -50.7) * mm, "end": v(-17.48, -49.82) * mm});
            skArc(sketch, "E296.MirrorCS", {"start": v(-17.48, -26.91) * mm, "mid": v(-16.16, -26.03) * mm, "end": v(-14.6, -25.72) * mm});
            skLineSegment(sketch, "E297.MirrorCS", {"start": v(-14.6, -25.72) * mm, "end": v(-10.2, -25.72) * mm});
            skArc(sketch, "E298.MirrorCS", {"start": v(-7.95, -25.04) * mm, "mid": v(-9.03, -25.55) * mm, "end": v(-10.2, -25.72) * mm});
            skArc(sketch, "E299.MirrorCS", {"start": v(-10.2, -51.01) * mm, "mid": v(-8.73, -51.29) * mm, "end": v(-7.46, -52.08) * mm});
            skLineSegment(sketch, "E300.MirrorCS", {"start": v(-27.5, -39.8) * mm, "end": v(-17.48, -49.82) * mm});
            skLineSegment(sketch, "E301.MirrorCS", {"start": v(-27.5, -36.93) * mm, "end": v(-17.48, -26.91) * mm});
            skLineSegment(sketch, "E302.MirrorCS", {"start": v(-14.6, -51.01) * mm, "end": v(-10.2, -51.01) * mm});
            skArc(sketch, "E303.MirrorCS", {"start": v(19.58, -52.58) * mm, "mid": v(19.08, -53.66) * mm, "end": v(18.9, -54.83) * mm});
            skArc(sketch, "E304.MirrorCS", {"start": v(19.58, -52.58) * mm, "mid": v(20.66, -52.07) * mm, "end": v(21.84, -51.9) * mm});
            skLineSegment(sketch, "E305.MirrorCS", {"start": v(26.24, -51.9) * mm, "end": v(21.84, -51.9) * mm});
            skLineSegment(sketch, "E306.MirrorCS", {"start": v(-6.38, -59.23) * mm, "end": v(-6.38, -54.83) * mm});
            skArc(sketch, "E307.MirrorCS", {"start": v(-6.38, -54.83) * mm, "mid": v(-6.66, -53.36) * mm, "end": v(-7.46, -52.08) * mm});
            skArc(sketch, "E308.MirrorCS", {"start": v(-6.38, -59.23) * mm, "mid": v(-6.07, -60.79) * mm, "end": v(-5.2, -62.1) * mm});
            skArc(sketch, "E309.MirrorCS", {"start": v(17.71, -62.1) * mm, "mid": v(18.6, -60.79) * mm, "end": v(18.9, -59.23) * mm});
            skLineSegment(sketch, "E310.MirrorCS", {"start": v(18.9, -59.23) * mm, "end": v(18.9, -54.83) * mm});
            skArc(sketch, "E311.MirrorCS", {"start": v(29.1, -50.7) * mm, "mid": v(27.8, -51.59) * mm, "end": v(26.24, -51.9) * mm});
            skArc(sketch, "E312.MirrorCS", {"start": v(26.24, -26.61) * mm, "mid": v(27.8, -26.92) * mm, "end": v(29.1, -27.8) * mm});
            skLineSegment(sketch, "E313.MirrorCS", {"start": v(22.3, -26.61) * mm, "end": v(21.84, -26.61) * mm});
            skLineSegment(sketch, "E314.MirrorCS", {"start": v(39.13, -37.82) * mm, "end": v(29.1, -27.8) * mm});
            skLineSegment(sketch, "E315.MirrorCS", {"start": v(39.13, -40.7) * mm, "end": v(29.1, -50.7) * mm});
            skLineSegment(sketch, "E316.MirrorCS", {"start": v(7.7, -72.12) * mm, "end": v(17.71, -62.1) * mm});
            skLineSegment(sketch, "E317.MirrorCS", {"start": v(4.82, -72.12) * mm, "end": v(-5.2, -62.1) * mm});
            skArc(sketch, "E318", {"start": v(18.02, -22.8) * mm, "mid": v(19.13, -25.5) * mm, "end": v(21.84, -26.61) * mm});
            skLineSegment(sketch, "E319", {"start": v(6.8, -5.5) * mm, "end": v(3.94, -5.5) * mm});
            skLineSegment(sketch, "E320", {"start": v(-27.5, -36.93) * mm, "end": v(-27.5, -39.8) * mm});
            skLineSegment(sketch, "E321", {"start": v(4.82, -72.12) * mm, "end": v(7.7, -72.12) * mm});
            skLineSegment(sketch, "E322", {"start": v(39.13, -37.82) * mm, "end": v(39.13, -40.7) * mm});
            skArc(sketch, "E323.MirrorCS", {"start": v(94.3, -25.04) * mm, "mid": v(95.37, -25.55) * mm, "end": v(96.55, -25.72) * mm});
            skArc(sketch, "E324.MirrorCS", {"start": v(66.76, -52.58) * mm, "mid": v(65.69, -52.07) * mm, "end": v(64.5, -51.9) * mm});
            skArc(sketch, "E325.MirrorCS", {"start": v(66.76, -52.58) * mm, "mid": v(67.27, -53.66) * mm, "end": v(67.44, -54.83) * mm});
            skArc(sketch, "E326.MirrorCS", {"start": v(94.3, -25.04) * mm, "mid": v(93.8, -23.97) * mm, "end": v(93.62, -22.8) * mm});
            skLineSegment(sketch, "E327.MirrorCS", {"start": v(60.11, -26.61) * mm, "end": v(64.5, -26.61) * mm});
            skLineSegment(sketch, "E328.MirrorCS", {"start": v(100.95, -25.72) * mm, "end": v(96.55, -25.72) * mm});
            skArc(sketch, "E329.MirrorCS", {"start": v(68.33, -18.4) * mm, "mid": v(68.64, -16.84) * mm, "end": v(69.52, -15.52) * mm});
            skArc(sketch, "E330.MirrorCS", {"start": v(92.73, -54.83) * mm, "mid": v(93, -53.36) * mm, "end": v(93.8, -52.08) * mm});
            skArc(sketch, "E331.MirrorCS", {"start": v(60.11, -26.61) * mm, "mid": v(58.56, -26.92) * mm, "end": v(57.24, -27.8) * mm});
            skArc(sketch, "E332.MirrorCS", {"start": v(92.43, -15.52) * mm, "mid": v(93.3, -16.84) * mm, "end": v(93.62, -18.4) * mm});
            skLineSegment(sketch, "E333.MirrorCS", {"start": v(68.33, -18.4) * mm, "end": v(68.33, -22.8) * mm});
            skLineSegment(sketch, "E334.MirrorCS", {"start": v(93.62, -18.4) * mm, "end": v(93.62, -22.8) * mm});
            skLineSegment(sketch, "E335.MirrorCS", {"start": v(67.44, -59.23) * mm, "end": v(67.44, -54.83) * mm});
            skArc(sketch, "E336.MirrorCS", {"start": v(96.55, -51.01) * mm, "mid": v(95.08, -51.29) * mm, "end": v(93.8, -52.08) * mm});
            skArc(sketch, "E337.MirrorCS", {"start": v(68.33, -22.8) * mm, "mid": v(67.21, -25.5) * mm, "end": v(64.5, -26.61) * mm});
            skArc(sketch, "E338.MirrorCS", {"start": v(100.95, -51.01) * mm, "mid": v(102.5, -50.7) * mm, "end": v(103.82, -49.82) * mm});
            skLineSegment(sketch, "E339.MirrorCS", {"start": v(113.84, -36.93) * mm, "end": v(113.84, -39.8) * mm});
            skLineSegment(sketch, "E340.MirrorCS", {"start": v(79.54, -5.5) * mm, "end": v(82.41, -5.5) * mm});
            skArc(sketch, "E341.MirrorCS", {"start": v(68.63, -62.1) * mm, "mid": v(67.75, -60.79) * mm, "end": v(67.44, -59.23) * mm});
            skLineSegment(sketch, "E342.MirrorCS", {"start": v(92.73, -59.23) * mm, "end": v(92.73, -54.83) * mm});
            skLineSegment(sketch, "E343.MirrorCS", {"start": v(47.22, -37.82) * mm, "end": v(47.22, -40.7) * mm});
            skArc(sketch, "E344.MirrorCS", {"start": v(103.82, -26.91) * mm, "mid": v(102.5, -26.03) * mm, "end": v(100.95, -25.72) * mm});
            skLineSegment(sketch, "E345.MirrorCS", {"start": v(60.11, -51.9) * mm, "end": v(64.5, -51.9) * mm});
            skLineSegment(sketch, "E346.MirrorCS", {"start": v(81.52, -72.12) * mm, "end": v(78.65, -72.12) * mm});
            skArc(sketch, "E347.MirrorCS", {"start": v(92.73, -59.23) * mm, "mid": v(92.42, -60.79) * mm, "end": v(91.54, -62.1) * mm});
            skLineSegment(sketch, "E348.MirrorCS", {"start": v(100.95, -51.01) * mm, "end": v(96.55, -51.01) * mm});
            skArc(sketch, "E349.MirrorCS", {"start": v(57.24, -50.7) * mm, "mid": v(58.56, -51.59) * mm, "end": v(60.11, -51.9) * mm});
            skLineSegment(sketch, "E350.MirrorCS", {"start": v(79.54, -5.5) * mm, "end": v(69.52, -15.52) * mm});
            skLineSegment(sketch, "E351.MirrorCS", {"start": v(81.52, -72.12) * mm, "end": v(91.54, -62.1) * mm});
            skLineSegment(sketch, "E352.MirrorCS", {"start": v(78.65, -72.12) * mm, "end": v(68.63, -62.1) * mm});
            skLineSegment(sketch, "E353.MirrorCS", {"start": v(113.84, -39.8) * mm, "end": v(103.82, -49.82) * mm});
            skLineSegment(sketch, "E354.MirrorCS", {"start": v(82.41, -5.5) * mm, "end": v(92.43, -15.52) * mm});
            skLineSegment(sketch, "E355.MirrorCS", {"start": v(47.22, -37.82) * mm, "end": v(57.24, -27.8) * mm});
            skLineSegment(sketch, "E356.MirrorCS", {"start": v(47.22, -40.7) * mm, "end": v(57.24, -50.7) * mm});
            skLineSegment(sketch, "E357.MirrorCS", {"start": v(113.84, -36.93) * mm, "end": v(103.82, -26.91) * mm});
            skLineSegment(sketch, "E358.MirrorCS", {"start": v(41.74, -5.5) * mm, "end": v(44.61, -5.5) * mm});
            skArc(sketch, "E359.MirrorCS", {"start": v(54.63, -15.52) * mm, "mid": v(55.5, -16.84) * mm, "end": v(55.82, -18.4) * mm});
            skLineSegment(sketch, "E360.MirrorCS", {"start": v(22.3, -26.61) * mm, "end": v(26.24, -26.61) * mm});
            skLineSegment(sketch, "E361.MirrorCS", {"start": v(30.53, -18.4) * mm, "end": v(30.53, -20.6) * mm});
            skArc(sketch, "E362.MirrorCS", {"start": v(30.53, -18.4) * mm, "mid": v(30.84, -16.84) * mm, "end": v(31.72, -15.52) * mm});
            skLineSegment(sketch, "E363.MirrorCS", {"start": v(44.61, -5.5) * mm, "end": v(54.63, -15.52) * mm});
            skLineSegment(sketch, "E364.MirrorCS", {"start": v(55.82, -18.4) * mm, "end": v(55.82, -20.6) * mm});
            skLineSegment(sketch, "E365.MirrorCS", {"start": v(41.74, -5.5) * mm, "end": v(31.72, -15.52) * mm});
            skLineSegment(sketch, "E366.MirrorCS", {"start": v(41.74, -35.68) * mm, "end": v(44.61, -35.68) * mm});
            skLineSegment(sketch, "E367.MirrorCS", {"start": v(55.82, -22.8) * mm, "end": v(55.82, -20.6) * mm});
            skLineSegment(sketch, "E368.MirrorCS", {"start": v(30.53, -22.8) * mm, "end": v(30.53, -20.6) * mm});
            skLineSegment(sketch, "E369.MirrorCS", {"start": v(44.61, -35.68) * mm, "end": v(54.63, -25.66) * mm});
            skArc(sketch, "E370.MirrorCS", {"start": v(54.63, -25.66) * mm, "mid": v(55.5, -24.35) * mm, "end": v(55.82, -22.8) * mm});
            skArc(sketch, "E371.MirrorCS", {"start": v(30.53, -22.8) * mm, "mid": v(30.84, -24.35) * mm, "end": v(31.72, -25.66) * mm});
            skLineSegment(sketch, "E372.MirrorCS", {"start": v(41.74, -35.68) * mm, "end": v(31.72, -25.66) * mm});
            skLineSegment(sketch, "E373.MirrorCS", {"start": v(30.53, -58.34) * mm, "end": v(30.53, -56.14) * mm});
            skLineSegment(sketch, "E374.MirrorCS", {"start": v(30.53, -53.94) * mm, "end": v(30.53, -56.14) * mm});
            skLineSegment(sketch, "E375.MirrorCS", {"start": v(55.82, -53.94) * mm, "end": v(55.82, -56.14) * mm});
            skLineSegment(sketch, "E376.MirrorCS", {"start": v(55.82, -58.34) * mm, "end": v(55.82, -56.14) * mm});
            skLineSegment(sketch, "E377.MirrorCS", {"start": v(41.74, -71.23) * mm, "end": v(44.61, -71.23) * mm});
            skArc(sketch, "E378.MirrorCS", {"start": v(54.63, -61.22) * mm, "mid": v(55.5, -59.9) * mm, "end": v(55.82, -58.34) * mm});
            skArc(sketch, "E379.MirrorCS", {"start": v(30.53, -58.34) * mm, "mid": v(30.84, -59.9) * mm, "end": v(31.72, -61.22) * mm});
            skLineSegment(sketch, "E380.MirrorCS", {"start": v(41.74, -71.23) * mm, "end": v(31.72, -61.22) * mm});
            skLineSegment(sketch, "E381.MirrorCS", {"start": v(44.61, -71.23) * mm, "end": v(54.63, -61.22) * mm});
            skLineSegment(sketch, "E382.MirrorCS", {"start": v(44.61, -41.05) * mm, "end": v(54.63, -51.07) * mm});
            skLineSegment(sketch, "E383.MirrorCS", {"start": v(41.74, -41.05) * mm, "end": v(44.61, -41.05) * mm});
            skLineSegment(sketch, "E384.MirrorCS", {"start": v(41.74, -41.05) * mm, "end": v(31.72, -51.07) * mm});
            skArc(sketch, "E385.MirrorCS", {"start": v(30.53, -53.94) * mm, "mid": v(30.84, -52.39) * mm, "end": v(31.72, -51.07) * mm});
            skArc(sketch, "E386.MirrorCS", {"start": v(54.63, -51.07) * mm, "mid": v(55.5, -52.39) * mm, "end": v(55.82, -53.94) * mm});
            skSolve(sketch);
        }
        {
            var Q0;
            Q0 = qSketchRegion(id + "F2", true);
            extrude(context, id + "F3", {"entities" : qUnion([Q0]), "operationType" : NewBodyOperationType.REMOVE, "endBound" : BoundingType.THROUGH_ALL, "oppositeDirection" : true, "depth" : 25.4 * mm});
        }
        {
            var Q0;
            Q0=makeQuery(id+"F1.opExtrude","CAP_FACE",FACE,{"disambiguationData":[OSD([sQuery(id+"F0.wireOp",EDGE,"E0"),sQuery(id+"F0.wireOp",EDGE,"E1"),sQuery(id+"F0.wireOp",EDGE,"E2"),sQuery(id+"F0.wireOp",EDGE,"E3"),sQuery(id+"F0.wireOp",EDGE,"E4"),sQuery(id+"F0.wireOp",EDGE,"E5"),sQuery(id+"F0.wireOp",EDGE,"E6"),sQuery(id+"F0.wireOp",EDGE,"E7"),sQuery(id+"F0.wireOp",EDGE,"E8"),sQuery(id+"F0.wireOp",EDGE,"E9"),sQuery(id+"F0.wireOp",EDGE,"E10.filletArc"),sQuery(id+"F0.wireOp",EDGE,"E11.MirrorCS"),sQuery(id+"F0.wireOp",EDGE,"E12.MirrorCS"),sQuery(id+"F0.wireOp",EDGE,"E14.MirrorCS"),sQuery(id+"F0.wireOp",EDGE,"E15.MirrorCS"),sQuery(id+"F0.wireOp",EDGE,"E16.MirrorCS"),sQuery(id+"F0.wireOp",EDGE,"E17.MirrorCS"),sQuery(id+"F0.wireOp",EDGE,"E18.MirrorCS"),sQuery(id+"F0.wireOp",EDGE,"E19.MirrorCS"),sQuery(id+"F0.wireOp",EDGE,"E20.MirrorCS"),sQuery(id+"F0.wireOp",EDGE,"E21.MirrorCS"),sQuery(id+"F0.wireOp",EDGE,"E22.MirrorCS"),sQuery(id+"F0.wireOp",EDGE,"E23.MirrorCS"),sQuery(id+"F0.wireOp",EDGE,"E24.MirrorCS"),sQuery(id+"F0.wireOp",EDGE,"E25.MirrorCS"),sQuery(id+"F0.wireOp",EDGE,"E28.MirrorCS"),sQuery(id+"F0.wireOp",EDGE,"E29.MirrorCS"),sQuery(id+"F0.wireOp",EDGE,"E30.MirrorCS"),sQuery(id+"F0.wireOp",EDGE,"E31.MirrorCS"),sQuery(id+"F0.wireOp",EDGE,"E32.MirrorCS"),sQuery(id+"F0.wireOp",EDGE,"E33.MirrorCS"),sQuery(id+"F0.wireOp",EDGE,"E34.MirrorCS"),sQuery(id+"F0.wireOp",EDGE,"E35.MirrorCS"),sQuery(id+"F0.wireOp",EDGE,"E36.MirrorCS"),sQuery(id+"F0.wireOp",EDGE,"E37.MirrorCS"),sQuery(id+"F0.wireOp",EDGE,"E38.MirrorCS"),sQuery(id+"F0.wireOp",EDGE,"E39.MirrorCS"),sQuery(id+"F0.wireOp",EDGE,"E40.MirrorCS"),sQuery(id+"F0.wireOp",EDGE,"E41.MirrorCS"),sQuery(id+"F0.wireOp",EDGE,"E42.MirrorCS"),sQuery(id+"F0.wireOp",EDGE,"E43.MirrorCS"),sQuery(id+"F0.wireOp",EDGE,"E44.MirrorCS"),sQuery(id+"F0.wireOp",EDGE,"E45.MirrorCS"),sQuery(id+"F0.wireOp",EDGE,"E46.MirrorCS"),sQuery(id+"F0.wireOp",EDGE,"E47.MirrorCS"),sQuery(id+"F0.wireOp",EDGE,"E48.MirrorCS"),sQuery(id+"F0.wireOp",EDGE,"E49.MirrorCS"),sQuery(id+"F0.wireOp",EDGE,"E50.MirrorCS"),sQuery(id+"F0.wireOp",EDGE,"E51.MirrorCS"),sQuery(id+"F0.wireOp",EDGE,"E52.MirrorCS"),sQuery(id+"F0.wireOp",EDGE,"E53.MirrorCS"),sQuery(id+"F0.wireOp",EDGE,"E54.MirrorCS"),sQuery(id+"F0.wireOp",EDGE,"E55.MirrorCS"),sQuery(id+"F0.wireOp",EDGE,"E56.MirrorCS"),sQuery(id+"F0.wireOp",EDGE,"E58.MirrorCS"),sQuery(id+"F0.wireOp",EDGE,"E59.MirrorCS"),sQuery(id+"F0.wireOp",EDGE,"E60.MirrorCS"),sQuery(id+"F0.wireOp",EDGE,"E61.MirrorCS"),sQuery(id+"F0.wireOp",EDGE,"E62.MirrorCS"),sQuery(id+"F0.wireOp",EDGE,"E63.MirrorCS"),sQuery(id+"F0.wireOp",EDGE,"E64.MirrorCS"),sQuery(id+"F0.wireOp",EDGE,"E65.MirrorCS"),sQuery(id+"F0.wireOp",EDGE,"E66.MirrorCS"),sQuery(id+"F0.wireOp",EDGE,"E67.MirrorCS"),sQuery(id+"F0.wireOp",EDGE,"E68.MirrorCS"),sQuery(id+"F0.wireOp",EDGE,"E69.MirrorCS"),sQuery(id+"F0.wireOp",EDGE,"E70.MirrorCS"),sQuery(id+"F0.wireOp",EDGE,"E71.MirrorCS"),sQuery(id+"F0.wireOp",EDGE,"E72.MirrorCS"),sQuery(id+"F0.wireOp",EDGE,"E73.MirrorCS"),sQuery(id+"F0.wireOp",EDGE,"E74.MirrorCS"),sQuery(id+"F0.wireOp",EDGE,"E75.MirrorCS"),sQuery(id+"F0.wireOp",EDGE,"E76.MirrorCS"),sQuery(id+"F0.wireOp",EDGE,"E77.MirrorCS"),sQuery(id+"F0.wireOp",EDGE,"E78.MirrorCS"),sQuery(id+"F0.wireOp",EDGE,"E79.MirrorCS"),sQuery(id+"F0.wireOp",EDGE,"E80.MirrorCS"),sQuery(id+"F0.wireOp",EDGE,"E81.MirrorCS"),sQuery(id+"F0.wireOp",EDGE,"E82.MirrorCS"),sQuery(id+"F0.wireOp",EDGE,"E83.MirrorCS"),sQuery(id+"F0.wireOp",EDGE,"E84.MirrorCS"),sQuery(id+"F0.wireOp",EDGE,"E85.MirrorCS"),sQuery(id+"F0.wireOp",EDGE,"E86.MirrorCS"),sQuery(id+"F0.wireOp",EDGE,"E87.MirrorCS"),sQuery(id+"F0.wireOp",EDGE,"E93.filletArc"),sQuery(id+"F0.wireOp",EDGE,"E94"),sQuery(id+"F0.wireOp",EDGE,"E95.MirrorCS"),sQuery(id+"F0.wireOp",EDGE,"E96.MirrorCS"),sQuery(id+"F0.wireOp",EDGE,"E97.MirrorCS"),sQuery(id+"F0.wireOp",EDGE,"E98.MirrorCS"),sQuery(id+"F0.wireOp",EDGE,"E99.MirrorCS"),sQuery(id+"F0.wireOp",EDGE,"E100.MirrorCS"),sQuery(id+"F0.wireOp",EDGE,"E101.MirrorCS"),sQuery(id+"F0.wireOp",EDGE,"E102.MirrorCS"),sQuery(id+"F0.wireOp",EDGE,"E103.MirrorCS"),sQuery(id+"F0.wireOp",EDGE,"E104.MirrorCS"),sQuery(id+"F0.wireOp",EDGE,"E105.MirrorCS"),sQuery(id+"F0.wireOp",EDGE,"E106.MirrorCS"),sQuery(id+"F0.wireOp",EDGE,"E107.MirrorCS"),sQuery(id+"F0.wireOp",EDGE,"E108.MirrorCS"),sQuery(id+"F0.wireOp",EDGE,"E109.MirrorCS"),sQuery(id+"F0.wireOp",EDGE,"E110.MirrorCS"),sQuery(id+"F0.wireOp",EDGE,"E111.MirrorCS"),sQuery(id+"F0.wireOp",EDGE,"E112.MirrorCS"),sQuery(id+"F0.wireOp",EDGE,"E113.MirrorCS"),sQuery(id+"F0.wireOp",EDGE,"E114.MirrorCS"),sQuery(id+"F0.wireOp",EDGE,"E115.MirrorCS"),sQuery(id+"F0.wireOp",EDGE,"E118.MirrorCS"),sQuery(id+"F0.wireOp",EDGE,"E119.MirrorCS"),sQuery(id+"F0.wireOp",EDGE,"E120.MirrorCS"),sQuery(id+"F0.wireOp",EDGE,"E121.MirrorCS"),sQuery(id+"F0.wireOp",EDGE,"E122.MirrorCS"),sQuery(id+"F0.wireOp",EDGE,"E123.MirrorCS"),sQuery(id+"F0.wireOp",EDGE,"E124.MirrorCS"),sQuery(id+"F0.wireOp",EDGE,"E127.MirrorCS"),sQuery(id+"F0.wireOp",EDGE,"E128.MirrorCS"),sQuery(id+"F0.wireOp",EDGE,"E129.MirrorCS"),sQuery(id+"F0.wireOp",EDGE,"E130.MirrorCS"),sQuery(id+"F0.wireOp",EDGE,"E131.MirrorCS"),sQuery(id+"F0.wireOp",EDGE,"E132.MirrorCS"),sQuery(id+"F0.wireOp",EDGE,"E133.MirrorCS"),sQuery(id+"F0.wireOp",EDGE,"E134.MirrorCS"),sQuery(id+"F0.wireOp",EDGE,"E135.MirrorCS"),sQuery(id+"F0.wireOp",EDGE,"E136.MirrorCS"),sQuery(id+"F0.wireOp",EDGE,"E137.MirrorCS"),sQuery(id+"F0.wireOp",EDGE,"E138.MirrorCS"),sQuery(id+"F0.wireOp",EDGE,"E139.MirrorCS"),sQuery(id+"F0.wireOp",EDGE,"E140.MirrorCS"),sQuery(id+"F0.wireOp",EDGE,"E141.MirrorCS"),sQuery(id+"F0.wireOp",EDGE,"E142"),sQuery(id+"F0.wireOp",EDGE,"E143.MirrorCS"),sQuery(id+"F0.wireOp",EDGE,"E144.MirrorCS"),sQuery(id+"F0.wireOp",EDGE,"E145.MirrorCS"),sQuery(id+"F0.wireOp",EDGE,"E146.MirrorCS"),sQuery(id+"F0.wireOp",EDGE,"E147.MirrorCS"),sQuery(id+"F0.wireOp",EDGE,"E148.MirrorCS"),sQuery(id+"F0.wireOp",EDGE,"E149.MirrorCS"),sQuery(id+"F0.wireOp",EDGE,"E150.MirrorCS"),sQuery(id+"F0.wireOp",EDGE,"E151.MirrorCS"),sQuery(id+"F0.wireOp",EDGE,"E152.MirrorCS"),sQuery(id+"F0.wireOp",EDGE,"E153.MirrorCS"),sQuery(id+"F0.wireOp",EDGE,"E154.MirrorCS"),sQuery(id+"F0.wireOp",EDGE,"E155.MirrorCS"),sQuery(id+"F0.wireOp",EDGE,"E156.MirrorCS"),sQuery(id+"F0.wireOp",EDGE,"E157.MirrorCS"),sQuery(id+"F0.wireOp",EDGE,"E158.MirrorCS"),sQuery(id+"F0.wireOp",EDGE,"E159.MirrorCS"),sQuery(id+"F0.wireOp",EDGE,"E160.MirrorCS"),sQuery(id+"F0.wireOp",EDGE,"E161.MirrorCS"),sQuery(id+"F0.wireOp",EDGE,"E162.MirrorCS"),sQuery(id+"F0.wireOp",EDGE,"E163.MirrorCS"),sQuery(id+"F0.wireOp",EDGE,"E164.MirrorCS"),sQuery(id+"F0.wireOp",EDGE,"E165.MirrorCS"),sQuery(id+"F0.wireOp",EDGE,"E166.MirrorCS"),sQuery(id+"F0.wireOp",EDGE,"E167.MirrorCS"),sQuery(id+"F0.wireOp",EDGE,"E168.MirrorCS"),sQuery(id+"F0.wireOp",EDGE,"E169.MirrorCS"),sQuery(id+"F0.wireOp",EDGE,"E170.MirrorCS"),sQuery(id+"F0.wireOp",EDGE,"E171.MirrorCS"),sQuery(id+"F0.wireOp",EDGE,"E172.MirrorCS"),sQuery(id+"F0.wireOp",EDGE,"E173.MirrorCS"),sQuery(id+"F0.wireOp",EDGE,"E174.MirrorCS"),sQuery(id+"F0.wireOp",EDGE,"E175.MirrorCS"),sQuery(id+"F0.wireOp",EDGE,"E176.MirrorCS"),sQuery(id+"F0.wireOp",EDGE,"E177.MirrorCS"),sQuery(id+"F0.wireOp",EDGE,"E178.MirrorCS"),sQuery(id+"F0.wireOp",EDGE,"E179.MirrorCS"),sQuery(id+"F0.wireOp",EDGE,"E180.MirrorCS"),sQuery(id+"F0.wireOp",EDGE,"E181.MirrorCS"),sQuery(id+"F0.wireOp",EDGE,"E182.MirrorCS"),sQuery(id+"F0.wireOp",EDGE,"E183.MirrorCS"),sQuery(id+"F0.wireOp",EDGE,"E184.MirrorCS"),sQuery(id+"F0.wireOp",EDGE,"E185.MirrorCS"),sQuery(id+"F0.wireOp",EDGE,"E186.MirrorCS"),sQuery(id+"F0.wireOp",EDGE,"E187.MirrorCS"),sQuery(id+"F0.wireOp",EDGE,"E188.MirrorCS"),sQuery(id+"F0.wireOp",EDGE,"E189.MirrorCS"),sQuery(id+"F0.wireOp",EDGE,"E190.MirrorCS"),sQuery(id+"F0.wireOp",EDGE,"E191.MirrorCS"),sQuery(id+"F0.wireOp",EDGE,"E192.MirrorCS"),sQuery(id+"F0.wireOp",EDGE,"E193.MirrorCS"),sQuery(id+"F0.wireOp",EDGE,"E194.MirrorCS"),sQuery(id+"F0.wireOp",EDGE,"E195.MirrorCS"),sQuery(id+"F0.wireOp",EDGE,"E196.MirrorCS"),sQuery(id+"F0.wireOp",EDGE,"E197.MirrorCS"),sQuery(id+"F0.wireOp",EDGE,"E198.MirrorCS"),sQuery(id+"F0.wireOp",EDGE,"E199.MirrorCS"),sQuery(id+"F0.wireOp",EDGE,"E200.MirrorCS"),sQuery(id+"F0.wireOp",EDGE,"E201.MirrorCS"),sQuery(id+"F0.wireOp",EDGE,"E202.MirrorCS"),sQuery(id+"F0.wireOp",EDGE,"E203.MirrorCS"),sQuery(id+"F0.wireOp",EDGE,"E204.MirrorCS"),sQuery(id+"F0.wireOp",EDGE,"E205.MirrorCS"),sQuery(id+"F0.wireOp",EDGE,"E206.MirrorCS"),sQuery(id+"F0.wireOp",EDGE,"E207.MirrorCS"),sQuery(id+"F0.wireOp",EDGE,"E208.MirrorCS"),sQuery(id+"F0.wireOp",EDGE,"E209.MirrorCS"),sQuery(id+"F0.wireOp",EDGE,"E210.MirrorCS"),sQuery(id+"F0.wireOp",EDGE,"E211.MirrorCS"),sQuery(id+"F0.wireOp",EDGE,"E212.MirrorCS"),sQuery(id+"F0.wireOp",EDGE,"E213.MirrorCS"),sQuery(id+"F0.wireOp",EDGE,"E214.MirrorCS"),sQuery(id+"F0.wireOp",EDGE,"E215.MirrorCS"),sQuery(id+"F0.wireOp",EDGE,"E216.MirrorCS"),sQuery(id+"F0.wireOp",EDGE,"E217.MirrorCS"),sQuery(id+"F0.wireOp",EDGE,"E218.MirrorCS"),sQuery(id+"F0.wireOp",EDGE,"E219.MirrorCS"),sQuery(id+"F0.wireOp",EDGE,"E220.MirrorCS"),sQuery(id+"F0.wireOp",EDGE,"E221.MirrorCS"),sQuery(id+"F0.wireOp",EDGE,"E222.MirrorCS"),sQuery(id+"F0.wireOp",EDGE,"E223.MirrorCS"),sQuery(id+"F0.wireOp",EDGE,"E224.MirrorCS"),sQuery(id+"F0.wireOp",EDGE,"E225.MirrorCS"),sQuery(id+"F0.wireOp",EDGE,"E226.MirrorCS"),sQuery(id+"F0.wireOp",EDGE,"E227.MirrorCS"),sQuery(id+"F0.wireOp",EDGE,"E228.MirrorCS"),sQuery(id+"F0.wireOp",EDGE,"E229.MirrorCS"),sQuery(id+"F0.wireOp",EDGE,"E230.MirrorCS"),sQuery(id+"F0.wireOp",EDGE,"E231.MirrorCS"),sQuery(id+"F0.wireOp",EDGE,"E232.MirrorCS"),sQuery(id+"F0.wireOp",EDGE,"E233.MirrorCS"),sQuery(id+"F0.wireOp",EDGE,"E234.MirrorCS"),sQuery(id+"F0.wireOp",EDGE,"E235.MirrorCS"),sQuery(id+"F0.wireOp",EDGE,"E236.MirrorCS"),sQuery(id+"F0.wireOp",EDGE,"E237.MirrorCS"),sQuery(id+"F0.wireOp",EDGE,"E238.MirrorCS"),sQuery(id+"F0.wireOp",EDGE,"E239.MirrorCS"),sQuery(id+"F0.wireOp",EDGE,"E240.MirrorCS"),sQuery(id+"F0.wireOp",EDGE,"E241.MirrorCS"),sQuery(id+"F0.wireOp",EDGE,"E242.MirrorCS"),sQuery(id+"F0.wireOp",EDGE,"E243.MirrorCS"),sQuery(id+"F0.wireOp",EDGE,"E244.MirrorCS"),sQuery(id+"F0.wireOp",EDGE,"E245.MirrorCS"),sQuery(id+"F0.wireOp",EDGE,"E246.MirrorCS"),sQuery(id+"F0.wireOp",EDGE,"E247.MirrorCS"),sQuery(id+"F0.wireOp",EDGE,"E248.MirrorCS"),sQuery(id+"F0.wireOp",EDGE,"E249.MirrorCS"),sQuery(id+"F0.wireOp",EDGE,"E250.MirrorCS"),sQuery(id+"F0.wireOp",EDGE,"E251.MirrorCS"),sQuery(id+"F0.wireOp",EDGE,"E252.MirrorCS"),sQuery(id+"F0.wireOp",EDGE,"E253.MirrorCS"),sQuery(id+"F0.wireOp",EDGE,"E254.MirrorCS"),sQuery(id+"F0.wireOp",EDGE,"E255.MirrorCS"),sQuery(id+"F0.wireOp",EDGE,"E256.MirrorCS"),sQuery(id+"F0.wireOp",EDGE,"E257.MirrorCS"),sQuery(id+"F0.wireOp",EDGE,"E258.MirrorCS"),sQuery(id+"F0.wireOp",EDGE,"E259.MirrorCS"),sQuery(id+"F0.wireOp",EDGE,"E260.MirrorCS"),sQuery(id+"F0.wireOp",EDGE,"E261.MirrorCS"),sQuery(id+"F0.wireOp",EDGE,"E262.MirrorCS"),sQuery(id+"F0.wireOp",EDGE,"E263.MirrorCS"),sQuery(id+"F0.wireOp",EDGE,"E264.MirrorCS"),sQuery(id+"F0.wireOp",EDGE,"E265.MirrorCS"),sQuery(id+"F0.wireOp",EDGE,"E268.MirrorCS"),sQuery(id+"F0.wireOp",EDGE,"E269.MirrorCS"),sQuery(id+"F0.wireOp",EDGE,"E275.MirrorCS"),sQuery(id+"F0.wireOp",EDGE,"E277.MirrorCS"),sQuery(id+"F0.wireOp",EDGE,"E280.MirrorCS"),sQuery(id+"F0.wireOp",EDGE,"E284.MirrorCS"),sQuery(id+"F0.wireOp",EDGE,"E287.MirrorCS")])],"isStart":false});
            var sketch = newSketch(context, id + "F4", { "sketchPlane" : qUnion([Q0])});
            skPoint(sketch, "E387", {"position": v(-13.95, -19.05) * mm});
            skPoint(sketch, "E388", {"position": v(-13.95, -57.15) * mm});
            skPoint(sketch, "E389", {"position": v(24.15, -19.05) * mm});
            skPoint(sketch, "E390", {"position": v(23.57, -57.15) * mm});
            skPoint(sketch, "E391", {"position": v(62.25, -19.05) * mm});
            skPoint(sketch, "E392", {"position": v(62.81, -57.15) * mm});
            skPoint(sketch, "E393", {"position": v(100.35, -19.05) * mm});
            skPoint(sketch, "E394", {"position": v(100.35, -57.15) * mm});
            skSolve(sketch);
        }
        {
            var Q0;
            Q0=sQuery(id+"F4.wireOp",VERTEX,"E387");
            var Q1;
            Q1=sQuery(id+"F4.wireOp",VERTEX,"E388");
            var Q2;
            Q2=sQuery(id+"F4.wireOp",VERTEX,"E390");
            var Q3;
            Q3=sQuery(id+"F4.wireOp",VERTEX,"E389");
            var Q4;
            Q4=sQuery(id+"F4.wireOp",VERTEX,"E391");
            var Q5;
            Q5=sQuery(id+"F4.wireOp",VERTEX,"E392");
            var Q6;
            Q6=sQuery(id+"F4.wireOp",VERTEX,"E393");
            var Q7;
            Q7=sQuery(id+"F4.wireOp",VERTEX,"E394");
            var Q8;
            Q8=makeQuery(id+"F1.opExtrude","SWEPT_BODY",BODY,{"disambiguationData":[OSD([sQuery(id+"F0.wireOp",EDGE,"E0"),sQuery(id+"F0.wireOp",EDGE,"E1"),sQuery(id+"F0.wireOp",EDGE,"E2"),sQuery(id+"F0.wireOp",EDGE,"E3"),sQuery(id+"F0.wireOp",EDGE,"E4"),sQuery(id+"F0.wireOp",EDGE,"E5"),sQuery(id+"F0.wireOp",EDGE,"E6"),sQuery(id+"F0.wireOp",EDGE,"E7"),sQuery(id+"F0.wireOp",EDGE,"E8"),sQuery(id+"F0.wireOp",EDGE,"E9"),sQuery(id+"F0.wireOp",EDGE,"E10.filletArc"),sQuery(id+"F0.wireOp",EDGE,"E11.MirrorCS"),sQuery(id+"F0.wireOp",EDGE,"E12.MirrorCS"),sQuery(id+"F0.wireOp",EDGE,"E14.MirrorCS"),sQuery(id+"F0.wireOp",EDGE,"E15.MirrorCS"),sQuery(id+"F0.wireOp",EDGE,"E16.MirrorCS"),sQuery(id+"F0.wireOp",EDGE,"E17.MirrorCS"),sQuery(id+"F0.wireOp",EDGE,"E18.MirrorCS"),sQuery(id+"F0.wireOp",EDGE,"E19.MirrorCS"),sQuery(id+"F0.wireOp",EDGE,"E20.MirrorCS"),sQuery(id+"F0.wireOp",EDGE,"E21.MirrorCS"),sQuery(id+"F0.wireOp",EDGE,"E22.MirrorCS"),sQuery(id+"F0.wireOp",EDGE,"E23.MirrorCS"),sQuery(id+"F0.wireOp",EDGE,"E24.MirrorCS"),sQuery(id+"F0.wireOp",EDGE,"E25.MirrorCS"),sQuery(id+"F0.wireOp",EDGE,"E28.MirrorCS"),sQuery(id+"F0.wireOp",EDGE,"E29.MirrorCS"),sQuery(id+"F0.wireOp",EDGE,"E30.MirrorCS"),sQuery(id+"F0.wireOp",EDGE,"E31.MirrorCS"),sQuery(id+"F0.wireOp",EDGE,"E32.MirrorCS"),sQuery(id+"F0.wireOp",EDGE,"E33.MirrorCS"),sQuery(id+"F0.wireOp",EDGE,"E34.MirrorCS"),sQuery(id+"F0.wireOp",EDGE,"E35.MirrorCS"),sQuery(id+"F0.wireOp",EDGE,"E36.MirrorCS"),sQuery(id+"F0.wireOp",EDGE,"E37.MirrorCS"),sQuery(id+"F0.wireOp",EDGE,"E38.MirrorCS"),sQuery(id+"F0.wireOp",EDGE,"E39.MirrorCS"),sQuery(id+"F0.wireOp",EDGE,"E40.MirrorCS"),sQuery(id+"F0.wireOp",EDGE,"E41.MirrorCS"),sQuery(id+"F0.wireOp",EDGE,"E42.MirrorCS"),sQuery(id+"F0.wireOp",EDGE,"E43.MirrorCS"),sQuery(id+"F0.wireOp",EDGE,"E44.MirrorCS"),sQuery(id+"F0.wireOp",EDGE,"E45.MirrorCS"),sQuery(id+"F0.wireOp",EDGE,"E46.MirrorCS"),sQuery(id+"F0.wireOp",EDGE,"E47.MirrorCS"),sQuery(id+"F0.wireOp",EDGE,"E48.MirrorCS"),sQuery(id+"F0.wireOp",EDGE,"E49.MirrorCS"),sQuery(id+"F0.wireOp",EDGE,"E50.MirrorCS"),sQuery(id+"F0.wireOp",EDGE,"E51.MirrorCS"),sQuery(id+"F0.wireOp",EDGE,"E52.MirrorCS"),sQuery(id+"F0.wireOp",EDGE,"E53.MirrorCS"),sQuery(id+"F0.wireOp",EDGE,"E54.MirrorCS"),sQuery(id+"F0.wireOp",EDGE,"E55.MirrorCS"),sQuery(id+"F0.wireOp",EDGE,"E56.MirrorCS"),sQuery(id+"F0.wireOp",EDGE,"E58.MirrorCS"),sQuery(id+"F0.wireOp",EDGE,"E59.MirrorCS"),sQuery(id+"F0.wireOp",EDGE,"E60.MirrorCS"),sQuery(id+"F0.wireOp",EDGE,"E61.MirrorCS"),sQuery(id+"F0.wireOp",EDGE,"E62.MirrorCS"),sQuery(id+"F0.wireOp",EDGE,"E63.MirrorCS"),sQuery(id+"F0.wireOp",EDGE,"E64.MirrorCS"),sQuery(id+"F0.wireOp",EDGE,"E65.MirrorCS"),sQuery(id+"F0.wireOp",EDGE,"E66.MirrorCS"),sQuery(id+"F0.wireOp",EDGE,"E67.MirrorCS"),sQuery(id+"F0.wireOp",EDGE,"E68.MirrorCS"),sQuery(id+"F0.wireOp",EDGE,"E69.MirrorCS"),sQuery(id+"F0.wireOp",EDGE,"E70.MirrorCS"),sQuery(id+"F0.wireOp",EDGE,"E71.MirrorCS"),sQuery(id+"F0.wireOp",EDGE,"E72.MirrorCS"),sQuery(id+"F0.wireOp",EDGE,"E73.MirrorCS"),sQuery(id+"F0.wireOp",EDGE,"E74.MirrorCS"),sQuery(id+"F0.wireOp",EDGE,"E75.MirrorCS"),sQuery(id+"F0.wireOp",EDGE,"E76.MirrorCS"),sQuery(id+"F0.wireOp",EDGE,"E77.MirrorCS"),sQuery(id+"F0.wireOp",EDGE,"E78.MirrorCS"),sQuery(id+"F0.wireOp",EDGE,"E79.MirrorCS"),sQuery(id+"F0.wireOp",EDGE,"E80.MirrorCS"),sQuery(id+"F0.wireOp",EDGE,"E81.MirrorCS"),sQuery(id+"F0.wireOp",EDGE,"E82.MirrorCS"),sQuery(id+"F0.wireOp",EDGE,"E83.MirrorCS"),sQuery(id+"F0.wireOp",EDGE,"E84.MirrorCS"),sQuery(id+"F0.wireOp",EDGE,"E85.MirrorCS"),sQuery(id+"F0.wireOp",EDGE,"E86.MirrorCS"),sQuery(id+"F0.wireOp",EDGE,"E87.MirrorCS"),sQuery(id+"F0.wireOp",EDGE,"E93.filletArc"),sQuery(id+"F0.wireOp",EDGE,"E94"),sQuery(id+"F0.wireOp",EDGE,"E95.MirrorCS"),sQuery(id+"F0.wireOp",EDGE,"E96.MirrorCS"),sQuery(id+"F0.wireOp",EDGE,"E97.MirrorCS"),sQuery(id+"F0.wireOp",EDGE,"E98.MirrorCS"),sQuery(id+"F0.wireOp",EDGE,"E99.MirrorCS"),sQuery(id+"F0.wireOp",EDGE,"E100.MirrorCS"),sQuery(id+"F0.wireOp",EDGE,"E101.MirrorCS"),sQuery(id+"F0.wireOp",EDGE,"E102.MirrorCS"),sQuery(id+"F0.wireOp",EDGE,"E103.MirrorCS"),sQuery(id+"F0.wireOp",EDGE,"E104.MirrorCS"),sQuery(id+"F0.wireOp",EDGE,"E105.MirrorCS"),sQuery(id+"F0.wireOp",EDGE,"E106.MirrorCS"),sQuery(id+"F0.wireOp",EDGE,"E107.MirrorCS"),sQuery(id+"F0.wireOp",EDGE,"E108.MirrorCS"),sQuery(id+"F0.wireOp",EDGE,"E109.MirrorCS"),sQuery(id+"F0.wireOp",EDGE,"E110.MirrorCS"),sQuery(id+"F0.wireOp",EDGE,"E111.MirrorCS"),sQuery(id+"F0.wireOp",EDGE,"E112.MirrorCS"),sQuery(id+"F0.wireOp",EDGE,"E113.MirrorCS"),sQuery(id+"F0.wireOp",EDGE,"E114.MirrorCS"),sQuery(id+"F0.wireOp",EDGE,"E115.MirrorCS"),sQuery(id+"F0.wireOp",EDGE,"E118.MirrorCS"),sQuery(id+"F0.wireOp",EDGE,"E119.MirrorCS"),sQuery(id+"F0.wireOp",EDGE,"E120.MirrorCS"),sQuery(id+"F0.wireOp",EDGE,"E121.MirrorCS"),sQuery(id+"F0.wireOp",EDGE,"E122.MirrorCS"),sQuery(id+"F0.wireOp",EDGE,"E123.MirrorCS"),sQuery(id+"F0.wireOp",EDGE,"E124.MirrorCS"),sQuery(id+"F0.wireOp",EDGE,"E127.MirrorCS"),sQuery(id+"F0.wireOp",EDGE,"E128.MirrorCS"),sQuery(id+"F0.wireOp",EDGE,"E129.MirrorCS"),sQuery(id+"F0.wireOp",EDGE,"E130.MirrorCS"),sQuery(id+"F0.wireOp",EDGE,"E131.MirrorCS"),sQuery(id+"F0.wireOp",EDGE,"E132.MirrorCS"),sQuery(id+"F0.wireOp",EDGE,"E133.MirrorCS"),sQuery(id+"F0.wireOp",EDGE,"E134.MirrorCS"),sQuery(id+"F0.wireOp",EDGE,"E135.MirrorCS"),sQuery(id+"F0.wireOp",EDGE,"E136.MirrorCS"),sQuery(id+"F0.wireOp",EDGE,"E137.MirrorCS"),sQuery(id+"F0.wireOp",EDGE,"E138.MirrorCS"),sQuery(id+"F0.wireOp",EDGE,"E139.MirrorCS"),sQuery(id+"F0.wireOp",EDGE,"E140.MirrorCS"),sQuery(id+"F0.wireOp",EDGE,"E141.MirrorCS"),sQuery(id+"F0.wireOp",EDGE,"E142"),sQuery(id+"F0.wireOp",EDGE,"E143.MirrorCS"),sQuery(id+"F0.wireOp",EDGE,"E144.MirrorCS"),sQuery(id+"F0.wireOp",EDGE,"E145.MirrorCS"),sQuery(id+"F0.wireOp",EDGE,"E146.MirrorCS"),sQuery(id+"F0.wireOp",EDGE,"E147.MirrorCS"),sQuery(id+"F0.wireOp",EDGE,"E148.MirrorCS"),sQuery(id+"F0.wireOp",EDGE,"E149.MirrorCS"),sQuery(id+"F0.wireOp",EDGE,"E150.MirrorCS"),sQuery(id+"F0.wireOp",EDGE,"E151.MirrorCS"),sQuery(id+"F0.wireOp",EDGE,"E152.MirrorCS"),sQuery(id+"F0.wireOp",EDGE,"E153.MirrorCS"),sQuery(id+"F0.wireOp",EDGE,"E154.MirrorCS"),sQuery(id+"F0.wireOp",EDGE,"E155.MirrorCS"),sQuery(id+"F0.wireOp",EDGE,"E156.MirrorCS"),sQuery(id+"F0.wireOp",EDGE,"E157.MirrorCS"),sQuery(id+"F0.wireOp",EDGE,"E158.MirrorCS"),sQuery(id+"F0.wireOp",EDGE,"E159.MirrorCS"),sQuery(id+"F0.wireOp",EDGE,"E160.MirrorCS"),sQuery(id+"F0.wireOp",EDGE,"E161.MirrorCS"),sQuery(id+"F0.wireOp",EDGE,"E162.MirrorCS"),sQuery(id+"F0.wireOp",EDGE,"E163.MirrorCS"),sQuery(id+"F0.wireOp",EDGE,"E164.MirrorCS"),sQuery(id+"F0.wireOp",EDGE,"E165.MirrorCS"),sQuery(id+"F0.wireOp",EDGE,"E166.MirrorCS"),sQuery(id+"F0.wireOp",EDGE,"E167.MirrorCS"),sQuery(id+"F0.wireOp",EDGE,"E168.MirrorCS"),sQuery(id+"F0.wireOp",EDGE,"E169.MirrorCS"),sQuery(id+"F0.wireOp",EDGE,"E170.MirrorCS"),sQuery(id+"F0.wireOp",EDGE,"E171.MirrorCS"),sQuery(id+"F0.wireOp",EDGE,"E172.MirrorCS"),sQuery(id+"F0.wireOp",EDGE,"E173.MirrorCS"),sQuery(id+"F0.wireOp",EDGE,"E174.MirrorCS"),sQuery(id+"F0.wireOp",EDGE,"E175.MirrorCS"),sQuery(id+"F0.wireOp",EDGE,"E176.MirrorCS"),sQuery(id+"F0.wireOp",EDGE,"E177.MirrorCS"),sQuery(id+"F0.wireOp",EDGE,"E178.MirrorCS"),sQuery(id+"F0.wireOp",EDGE,"E179.MirrorCS"),sQuery(id+"F0.wireOp",EDGE,"E180.MirrorCS"),sQuery(id+"F0.wireOp",EDGE,"E181.MirrorCS"),sQuery(id+"F0.wireOp",EDGE,"E182.MirrorCS"),sQuery(id+"F0.wireOp",EDGE,"E183.MirrorCS"),sQuery(id+"F0.wireOp",EDGE,"E184.MirrorCS"),sQuery(id+"F0.wireOp",EDGE,"E185.MirrorCS"),sQuery(id+"F0.wireOp",EDGE,"E186.MirrorCS"),sQuery(id+"F0.wireOp",EDGE,"E187.MirrorCS"),sQuery(id+"F0.wireOp",EDGE,"E188.MirrorCS"),sQuery(id+"F0.wireOp",EDGE,"E189.MirrorCS"),sQuery(id+"F0.wireOp",EDGE,"E190.MirrorCS"),sQuery(id+"F0.wireOp",EDGE,"E191.MirrorCS"),sQuery(id+"F0.wireOp",EDGE,"E192.MirrorCS"),sQuery(id+"F0.wireOp",EDGE,"E193.MirrorCS"),sQuery(id+"F0.wireOp",EDGE,"E194.MirrorCS"),sQuery(id+"F0.wireOp",EDGE,"E195.MirrorCS"),sQuery(id+"F0.wireOp",EDGE,"E196.MirrorCS"),sQuery(id+"F0.wireOp",EDGE,"E197.MirrorCS"),sQuery(id+"F0.wireOp",EDGE,"E198.MirrorCS"),sQuery(id+"F0.wireOp",EDGE,"E199.MirrorCS"),sQuery(id+"F0.wireOp",EDGE,"E200.MirrorCS"),sQuery(id+"F0.wireOp",EDGE,"E201.MirrorCS"),sQuery(id+"F0.wireOp",EDGE,"E202.MirrorCS"),sQuery(id+"F0.wireOp",EDGE,"E203.MirrorCS"),sQuery(id+"F0.wireOp",EDGE,"E204.MirrorCS"),sQuery(id+"F0.wireOp",EDGE,"E205.MirrorCS"),sQuery(id+"F0.wireOp",EDGE,"E206.MirrorCS"),sQuery(id+"F0.wireOp",EDGE,"E207.MirrorCS"),sQuery(id+"F0.wireOp",EDGE,"E208.MirrorCS"),sQuery(id+"F0.wireOp",EDGE,"E209.MirrorCS"),sQuery(id+"F0.wireOp",EDGE,"E210.MirrorCS"),sQuery(id+"F0.wireOp",EDGE,"E211.MirrorCS"),sQuery(id+"F0.wireOp",EDGE,"E212.MirrorCS"),sQuery(id+"F0.wireOp",EDGE,"E213.MirrorCS"),sQuery(id+"F0.wireOp",EDGE,"E214.MirrorCS"),sQuery(id+"F0.wireOp",EDGE,"E215.MirrorCS"),sQuery(id+"F0.wireOp",EDGE,"E216.MirrorCS"),sQuery(id+"F0.wireOp",EDGE,"E217.MirrorCS"),sQuery(id+"F0.wireOp",EDGE,"E218.MirrorCS"),sQuery(id+"F0.wireOp",EDGE,"E219.MirrorCS"),sQuery(id+"F0.wireOp",EDGE,"E220.MirrorCS"),sQuery(id+"F0.wireOp",EDGE,"E221.MirrorCS"),sQuery(id+"F0.wireOp",EDGE,"E222.MirrorCS"),sQuery(id+"F0.wireOp",EDGE,"E223.MirrorCS"),sQuery(id+"F0.wireOp",EDGE,"E224.MirrorCS"),sQuery(id+"F0.wireOp",EDGE,"E225.MirrorCS"),sQuery(id+"F0.wireOp",EDGE,"E226.MirrorCS"),sQuery(id+"F0.wireOp",EDGE,"E227.MirrorCS"),sQuery(id+"F0.wireOp",EDGE,"E228.MirrorCS"),sQuery(id+"F0.wireOp",EDGE,"E229.MirrorCS"),sQuery(id+"F0.wireOp",EDGE,"E230.MirrorCS"),sQuery(id+"F0.wireOp",EDGE,"E231.MirrorCS"),sQuery(id+"F0.wireOp",EDGE,"E232.MirrorCS"),sQuery(id+"F0.wireOp",EDGE,"E233.MirrorCS"),sQuery(id+"F0.wireOp",EDGE,"E234.MirrorCS"),sQuery(id+"F0.wireOp",EDGE,"E235.MirrorCS"),sQuery(id+"F0.wireOp",EDGE,"E236.MirrorCS"),sQuery(id+"F0.wireOp",EDGE,"E237.MirrorCS"),sQuery(id+"F0.wireOp",EDGE,"E238.MirrorCS"),sQuery(id+"F0.wireOp",EDGE,"E239.MirrorCS"),sQuery(id+"F0.wireOp",EDGE,"E240.MirrorCS"),sQuery(id+"F0.wireOp",EDGE,"E241.MirrorCS"),sQuery(id+"F0.wireOp",EDGE,"E242.MirrorCS"),sQuery(id+"F0.wireOp",EDGE,"E243.MirrorCS"),sQuery(id+"F0.wireOp",EDGE,"E244.MirrorCS"),sQuery(id+"F0.wireOp",EDGE,"E245.MirrorCS"),sQuery(id+"F0.wireOp",EDGE,"E246.MirrorCS"),sQuery(id+"F0.wireOp",EDGE,"E247.MirrorCS"),sQuery(id+"F0.wireOp",EDGE,"E248.MirrorCS"),sQuery(id+"F0.wireOp",EDGE,"E249.MirrorCS"),sQuery(id+"F0.wireOp",EDGE,"E250.MirrorCS"),sQuery(id+"F0.wireOp",EDGE,"E251.MirrorCS"),sQuery(id+"F0.wireOp",EDGE,"E252.MirrorCS"),sQuery(id+"F0.wireOp",EDGE,"E253.MirrorCS"),sQuery(id+"F0.wireOp",EDGE,"E254.MirrorCS"),sQuery(id+"F0.wireOp",EDGE,"E255.MirrorCS"),sQuery(id+"F0.wireOp",EDGE,"E256.MirrorCS"),sQuery(id+"F0.wireOp",EDGE,"E257.MirrorCS"),sQuery(id+"F0.wireOp",EDGE,"E258.MirrorCS"),sQuery(id+"F0.wireOp",EDGE,"E259.MirrorCS"),sQuery(id+"F0.wireOp",EDGE,"E260.MirrorCS"),sQuery(id+"F0.wireOp",EDGE,"E261.MirrorCS"),sQuery(id+"F0.wireOp",EDGE,"E262.MirrorCS"),sQuery(id+"F0.wireOp",EDGE,"E263.MirrorCS"),sQuery(id+"F0.wireOp",EDGE,"E264.MirrorCS"),sQuery(id+"F0.wireOp",EDGE,"E265.MirrorCS"),sQuery(id+"F0.wireOp",EDGE,"E268.MirrorCS"),sQuery(id+"F0.wireOp",EDGE,"E269.MirrorCS"),sQuery(id+"F0.wireOp",EDGE,"E275.MirrorCS"),sQuery(id+"F0.wireOp",EDGE,"E277.MirrorCS"),sQuery(id+"F0.wireOp",EDGE,"E280.MirrorCS"),sQuery(id+"F0.wireOp",EDGE,"E284.MirrorCS"),sQuery(id+"F0.wireOp",EDGE,"E287.MirrorCS")])]});
            hole(context, id + "F5", {"style" : HoleStyle.SIMPLE, "holeDiameter" : 5.1 * mm, "endStyle" : HoleEndStyle.THROUGH, "locations" : qUnion([Q0, Q1, Q2, Q3, Q4, Q5, Q6, Q7]), "scope" : qUnion([Q8])});
        }
    });
